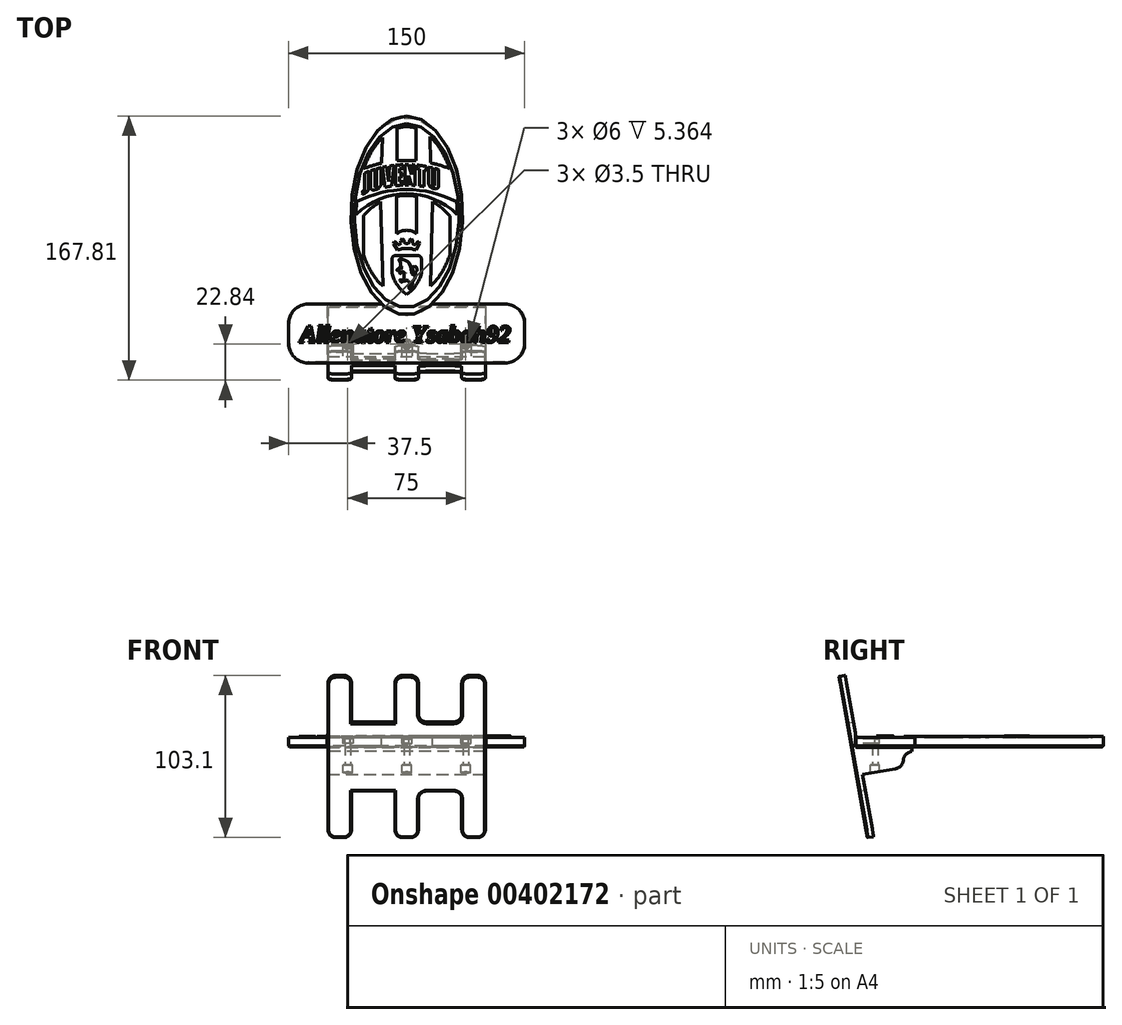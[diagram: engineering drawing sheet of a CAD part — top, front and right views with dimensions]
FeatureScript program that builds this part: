
annotation { "Feature Type Name" : "Feature", "Feature Type Description" : "" }
export const myFeature = defineFeature(function(context is Context, id is Id, definition is map)
    precondition{}
    {
        {
            var Q0;
            Q0=qCreatedBy(makeId("Top.planeOp"),FACE);
            var sketch = newSketch(context, id + "F0", { "sketchPlane" : qUnion([Q0])});
            skLineSegment(sketch, "E0", {"start": v(-0.23, 25.5) * mm, "end": v(16, 25.5) * mm, "construction": true});
            skLineSegment(sketch, "E1", {"start": v(0, -25.5) * mm, "end": v(11.3, -25.5) * mm, "construction": true});
            skLineSegment(sketch, "E2", {"start": v(14.52, 0) * mm, "end": v(14.52, -36.9) * mm, "construction": true});
            skLineSegment(sketch, "E3", {"start": v(-14.52, 0) * mm, "end": v(-14.52, -36.9) * mm, "construction": true});
            skEllipse(sketch, "E4", {"center": v(0, 0) * mm, "majorRadius": 14.2 * mm, "minorRadius": 25.29 * mm, "majorAxis": v(1, 0)});
            skEllipse(sketch, "E5", {"center": v(0, 0) * mm, "majorRadius": 13.32 * mm, "minorRadius": 23.36 * mm, "majorAxis": v(1, 0)});
            skEllipticalArc(sketch, "E6", {});
            skArc(sketch, "E7", {"start": v(-6.37, 13.3) * mm, "mid": v(-8.68, 12.68) * mm, "end": v(-10.93, 11.88) * mm});
            skLineSegment(sketch, "E8", {"start": v(-2.53, 14) * mm, "end": v(2.36, 14) * mm, "construction": true});
            skLineSegment(sketch, "E9", {"start": v(2.42, 22.16) * mm, "end": v(2.42, 13.9) * mm});
            skLineSegment(sketch, "E10", {"start": v(-2.48, 13.89) * mm, "end": v(-2.48, 22.14) * mm});
            skLineSegment(sketch, "E11", {"start": v(-6.2, 19.77) * mm, "end": v(-6.37, 13.3) * mm});
            skLineSegment(sketch, "E12", {"start": v(5.9, 20.05) * mm, "end": v(6, 13.37) * mm});
            skArc(sketch, "E13.trimOffspring", {"start": v(2.42, 13.9) * mm, "mid": v(-0.03, 14) * mm, "end": v(-2.48, 13.89) * mm});
            skEllipticalArc(sketch, "E14.trimOffspring", {});
            skArc(sketch, "E15.trimOffspring", {"start": v(10.93, 11.88) * mm, "mid": v(8.5, 12.73) * mm, "end": v(6, 13.37) * mm});
            skLineSegment(sketch, "E16", {"start": v(0, 6.57) * mm, "end": v(2.24, 6.57) * mm, "construction": true});
            skArc(sketch, "E17", {"start": v(12.7, 3.48) * mm, "mid": v(0, 6.57) * mm, "end": v(-12.7, 3.48) * mm});
            skLineSegment(sketch, "E18", {"start": v(0, 5.53) * mm, "end": v(1.97, 5.53) * mm, "construction": true});
            skArc(sketch, "E19", {"start": v(12.85, 0.22) * mm, "mid": v(0, 5.53) * mm, "end": v(-12.85, 0.22) * mm});
            skEllipticalArc(sketch, "E20.trimOffspring", {});
            skEllipticalArc(sketch, "E21.trimOffspring", {});
            skEllipticalArc(sketch, "E22", {});
            skLineSegment(sketch, "E23", {"start": v(0, 5.1) * mm, "end": v(2.87, 5.1) * mm, "construction": true});
            skLineSegment(sketch, "E24", {"start": v(11, -0.2) * mm, "end": v(11, -9.97) * mm});
            skLineSegment(sketch, "E25", {"start": v(6.52, 3.5) * mm, "end": v(6.04, -17.97) * mm});
            skLineSegment(sketch, "E26", {"start": v(-6.58, 3.47) * mm, "end": v(-6.04, -17.97) * mm});
            skLineSegment(sketch, "E27.MirrorCS", {"start": v(-11, -0.2) * mm, "end": v(-11, -9.97) * mm});
            skEllipticalArc(sketch, "E28.trimOffspring", {});
            skArc(sketch, "E29", {"start": v(2.52, -4.66) * mm, "mid": v(0, -3.77) * mm, "end": v(-2.52, -4.66) * mm});
            skLineSegment(sketch, "E30", {"start": v(2.52, 4.87) * mm, "end": v(2.52, -4.66) * mm});
            skLineSegment(sketch, "E31.MirrorCS", {"start": v(-2.52, 4.87) * mm, "end": v(-2.52, -4.66) * mm});
            skArc(sketch, "E32.trimOffspring", {"start": v(2.52, 4.87) * mm, "mid": v(0, 5.1) * mm, "end": v(-2.52, 4.87) * mm});
            skArc(sketch, "E33.trimOffspring", {"start": v(-6.58, 3.47) * mm, "mid": v(-8.99, 1.86) * mm, "end": v(-11, -0.2) * mm});
            skArc(sketch, "E34.trimOffspring", {"start": v(11, -0.2) * mm, "mid": v(8.96, 1.89) * mm, "end": v(6.52, 3.5) * mm});
            skEllipticalArc(sketch, "E35.trimOffspring", {});
            skArc(sketch, "E36", {"start": v(2.34, -8.82) * mm, "mid": v(0, -8.36) * mm, "end": v(-2.34, -8.82) * mm});
            skLineSegment(sketch, "E37", {"start": v(2.34, -8.82) * mm, "end": v(3.28, -7.14) * mm});
            skLineSegment(sketch, "E38", {"start": v(3.28, -7.14) * mm, "end": v(3.2, -6.62) * mm});
            skLineSegment(sketch, "E39", {"start": v(3.2, -6.62) * mm, "end": v(2.76, -6.8) * mm});
            skLineSegment(sketch, "E40", {"start": v(2.76, -6.8) * mm, "end": v(2.23, -7.36) * mm});
            skLineSegment(sketch, "E41", {"start": v(2.23, -7.36) * mm, "end": v(1.8, -7.36) * mm});
            skLineSegment(sketch, "E42", {"start": v(1.8, -7.36) * mm, "end": v(1.44, -7.04) * mm});
            skLineSegment(sketch, "E43", {"start": v(1.44, -7.04) * mm, "end": v(1.54, -6.32) * mm});
            skLineSegment(sketch, "E44", {"start": v(1.54, -6.32) * mm, "end": v(1.2, -5.88) * mm});
            skLineSegment(sketch, "E45", {"start": v(1.2, -5.88) * mm, "end": v(0.72, -6.24) * mm});
            skLineSegment(sketch, "E46", {"start": v(0.72, -6.24) * mm, "end": v(0.67, -6.78) * mm});
            skLineSegment(sketch, "E47", {"start": v(0.67, -6.78) * mm, "end": v(0.31, -7.14) * mm});
            skLineSegment(sketch, "E48", {"start": v(0.31, -7.14) * mm, "end": v(0, -7.14) * mm});
            skLineSegment(sketch, "E49", {"start": v(0, -8.36) * mm, "end": v(0, -5.24) * mm, "construction": true});
            skLineSegment(sketch, "E50.MirrorCS", {"start": v(-0.31, -7.14) * mm, "end": v(0, -7.14) * mm});
            skLineSegment(sketch, "E51.MirrorCS", {"start": v(-0.67, -6.78) * mm, "end": v(-0.31, -7.14) * mm});
            skLineSegment(sketch, "E52.MirrorCS", {"start": v(-0.72, -6.24) * mm, "end": v(-0.67, -6.78) * mm});
            skLineSegment(sketch, "E53.MirrorCS", {"start": v(-1.2, -5.88) * mm, "end": v(-0.72, -6.24) * mm});
            skLineSegment(sketch, "E54.MirrorCS", {"start": v(-1.54, -6.32) * mm, "end": v(-1.2, -5.88) * mm});
            skLineSegment(sketch, "E55.MirrorCS", {"start": v(-1.44, -7.04) * mm, "end": v(-1.54, -6.32) * mm});
            skLineSegment(sketch, "E56.MirrorCS", {"start": v(-1.8, -7.36) * mm, "end": v(-1.44, -7.04) * mm});
            skLineSegment(sketch, "E57.MirrorCS", {"start": v(-2.23, -7.36) * mm, "end": v(-1.8, -7.36) * mm});
            skLineSegment(sketch, "E58.MirrorCS", {"start": v(-2.76, -6.8) * mm, "end": v(-2.23, -7.36) * mm});
            skLineSegment(sketch, "E59.MirrorCS", {"start": v(-3.2, -6.62) * mm, "end": v(-2.76, -6.8) * mm});
            skLineSegment(sketch, "E60.MirrorCS", {"start": v(-2.34, -8.82) * mm, "end": v(-3.28, -7.14) * mm});
            skLineSegment(sketch, "E61.MirrorCS", {"start": v(-3.28, -7.14) * mm, "end": v(-3.2, -6.62) * mm});
            skLineSegment(sketch, "E62", {"start": v(3.75, -14.7) * mm, "end": v(3.75, -11.16) * mm});
            skLineSegment(sketch, "E63", {"start": v(0, -10.2) * mm, "end": v(3.06, -10.2) * mm});
            skArc(sketch, "E64", {"start": v(3.75, -11.16) * mm, "mid": v(3.57, -10.57) * mm, "end": v(3.06, -10.2) * mm});
            skLineSegment(sketch, "E65", {"start": v(0, -10.2) * mm, "end": v(0, -20.13) * mm, "construction": true});
            skArc(sketch, "E66.trimOffspring", {"start": v(0, -20.13) * mm, "mid": v(2.34, -17.73) * mm, "end": v(3.75, -14.7) * mm});
            skLineSegment(sketch, "E67.MirrorCS", {"start": v(-3.75, -14.7) * mm, "end": v(-3.75, -11.16) * mm});
            skLineSegment(sketch, "E68.MirrorCS", {"start": v(0, -10.2) * mm, "end": v(-3.06, -10.2) * mm});
            skArc(sketch, "E69.MirrorCS", {"start": v(-3.75, -11.16) * mm, "mid": v(-3.57, -10.57) * mm, "end": v(-3.06, -10.2) * mm});
            skArc(sketch, "E70.MirrorCS", {"start": v(0, -20.13) * mm, "mid": v(-2.34, -17.73) * mm, "end": v(-3.75, -14.7) * mm});
            skFitSpline(sketch, "E71", {"points": [v(2.15, -12.9) * mm, v(2.4, -13.22) * mm, v(2.4, -13.93) * mm, v(2.07, -13.78) * mm, v(1.97, -13.57) * mm, v(1.94, -13.4) * mm, v(1.95, -13.25) * mm, v(1.84, -13.17) * mm, v(1.77, -13.25) * mm, v(1.75, -13.35) * mm, v(1.76, -13.5) * mm, v(1.8, -13.68) * mm, v(1.9, -13.87) * mm, v(1.98, -14.07) * mm, v(2.08, -14.32) * mm, v(2.16, -14.54) * mm, v(2.2, -14.84) * mm, v(2.21, -14.95) * mm, v(2.27, -15.3) * mm, v(2.23, -15.56) * mm, v(2.12, -15.75) * mm, v(2.03, -15.92) * mm, v(1.95, -16.14) * mm, v(1.78, -16.38) * mm, v(1.73, -16.45) * mm, v(1.58, -16.7) * mm, v(1.5, -16.8) * mm, v(1.48, -16.97) * mm, v(1.5, -17.1) * mm, v(1.52, -17.2) * mm, v(1.62, -17.35) * mm, v(1.52, -17.51) * mm, v(1.31, -17.74) * mm, v(1.17, -17.96) * mm, v(1.12, -18.14) * mm, v(1.13, -18.28) * mm, v(1.24, -18.4) * mm, v(1.14, -18.66) * mm, v(1.03, -18.71) * mm, v(0.87, -18.73) * mm, v(0.69, -18.7) * mm, v(0.65, -18.63) * mm, v(0.63, -18.58) * mm, v(0.6, -18.5) * mm, v(0.57, -18.32) * mm, v(0.59, -18.14) * mm, v(0.61, -18.04) * mm, v(0.61, -17.96) * mm, v(0.63, -17.87) * mm, v(0.69, -17.8) * mm, v(0.77, -17.8) * mm, v(0.83, -17.76) * mm, v(0.83, -17.55) * mm, v(0.82, -17.33) * mm, v(0.74, -17.15) * mm, v(0.69, -17.06) * mm, v(0.64, -16.97) * mm, v(0.52, -16.78) * mm, v(0.44, -16.7) * mm, v(0.34, -16.53) * mm, v(0.26, -16.45) * mm, v(0.11, -16.36) * mm, v(0, -16.38) * mm, v(-0.12, -16.45) * mm, v(-0.27, -16.62) * mm, v(-0.38, -16.63) * mm, v(-0.61, -16.63) * mm, v(-0.63, -16.63) * mm], "startDerivative": vector(12.1, -9.46) * mm, "endDerivative": vector(-1.76, 0.05) * mm});
            skFitSpline(sketch, "E72", {"points": [v(-0.62, -16.63) * mm, v(-0.84, -16.63) * mm, v(-0.96, -16.63) * mm, v(-1.14, -16.63) * mm, v(-1.24, -16.65) * mm, v(-1.3, -16.74) * mm, v(-1.33, -16.89) * mm, v(-1.36, -16.97) * mm, v(-1.48, -17.04) * mm, v(-1.64, -17.01) * mm, v(-1.8, -16.91) * mm, v(-1.83, -16.76) * mm, v(-1.78, -16.57) * mm, v(-1.73, -16.45) * mm, v(-1.61, -16.36) * mm, v(-1.52, -16.3) * mm, v(-1.47, -16.28) * mm, v(-1.36, -16.27) * mm, v(-1.22, -16.2) * mm, v(-1.1, -16.19) * mm, v(-0.93, -16.18) * mm, v(-0.74, -16.17) * mm, v(-0.7, -15.94) * mm, v(-0.7, -15.8) * mm, v(-0.7, -15.55) * mm, v(-0.62, -15.33) * mm, v(-0.61, -15.15) * mm, v(-0.48, -14.95) * mm, v(0, -14.77) * mm, v(-0.51, -14.6) * mm, v(-0.67, -14.45) * mm, v(-0.87, -14.28) * mm, v(-1.05, -14.12) * mm, v(-1.23, -14.03) * mm, v(-1.32, -14.02) * mm, v(-1.4, -14.08) * mm, v(-1.43, -14.21) * mm, v(-1.35, -14.34) * mm, v(-1.24, -14.4) * mm, v(-1.17, -14.55) * mm, v(-1.2, -14.68) * mm, v(-1.24, -14.77) * mm, v(-1.35, -14.87) * mm, v(-1.48, -14.88) * mm, v(-1.6, -14.82) * mm, v(-1.75, -14.66) * mm, v(-1.8, -14.4) * mm, v(-1.78, -14.2) * mm, v(-1.74, -13.94) * mm, v(-1.8, -13.8) * mm, v(-1.85, -13.77) * mm, v(-1.97, -13.78) * mm, v(-2.07, -13.88) * mm, v(-2.11, -13.98) * mm, v(-2.15, -14.07) * mm, v(-2.2, -14.13) * mm, v(-2.35, -14.13) * mm, v(-2.4, -14.11) * mm, v(-2.48, -14.07) * mm, v(-2.52, -14) * mm, v(-2.53, -13.9) * mm, v(-2.48, -13.73) * mm, v(-2.42, -13.6) * mm, v(-2.38, -13.54) * mm, v(-2.28, -13.4) * mm, v(-2.15, -13.34) * mm, v(-2, -13.32) * mm, v(-1.93, -13.31) * mm, v(-1.86, -13.28) * mm, v(-1.83, -13.23) * mm, v(-1.78, -13.17) * mm, v(-1.68, -13.14) * mm, v(-1.56, -13.22) * mm, v(-1.44, -13.31) * mm, v(-1.29, -13.37) * mm, v(-1.24, -13.37) * mm, v(-1.14, -13.37) * mm, v(-1.05, -13.27) * mm, v(-1, -13.08) * mm, v(-1.08, -12.97) * mm, v(-1.3, -12.95) * mm, v(-1.42, -12.97) * mm, v(-1.52, -12.91) * mm, v(-1.54, -12.86) * mm, v(-1.58, -12.67) * mm, v(-1.56, -12.46) * mm, v(-1.53, -12.33) * mm, v(-1.5, -12.09) * mm, v(-1.49, -12.04) * mm, v(-1.53, -11.89) * mm, v(-1.64, -11.78) * mm, v(-1.66, -11.74) * mm, v(-1.73, -11.65) * mm, v(-1.75, -11.6) * mm, v(-1.77, -11.55) * mm, v(-1.8, -11.5) * mm, v(-1.84, -11.47) * mm, v(-1.94, -11.3) * mm, v(-1.94, -11.19) * mm, v(-1.81, -11.25) * mm, v(-1.76, -11.3) * mm, v(-1.66, -11.33) * mm, v(-1.62, -11.3) * mm, v(-1.68, -11.17) * mm, v(-1.73, -11.06) * mm, v(-1.73, -11) * mm, v(-1.64, -10.95) * mm, v(-1.6, -10.96) * mm, v(-1.47, -11.08) * mm, v(-1.33, -11.15) * mm, v(-1.1, -11.24) * mm, v(-0.94, -11.26) * mm, v(-0.71, -11.32) * mm, v(-0.58, -11.35) * mm, v(-0.41, -11.4) * mm, v(-0.25, -11.44) * mm, v(-0.2, -11.45) * mm, v(-0.12, -11.47) * mm, v(0.22, -11.64) * mm, v(0.43, -11.77) * mm, v(0.48, -11.8) * mm, v(0.54, -11.89) * mm, v(0.58, -11.93) * mm, v(0.63, -12.01) * mm, v(0.69, -12.14) * mm, v(0.72, -12.18) * mm, v(0.77, -12.32) * mm, v(0.96, -12.83) * mm, v(1.03, -13.13) * mm, v(1.15, -13.66) * mm, v(1.2, -13.92) * mm, v(1.22, -14.1) * mm, v(1.23, -14.25) * mm, v(1.32, -14.64) * mm, v(1.4, -14.83) * mm, v(1.47, -14.98) * mm, v(1.53, -15.05) * mm, v(1.64, -15.08) * mm, v(1.68, -15.08) * mm, v(1.74, -15.08) * mm, v(1.86, -15) * mm, v(1.87, -14.95) * mm, v(1.85, -14.8) * mm, v(1.8, -14.69) * mm, v(1.78, -14.65) * mm, v(1.75, -14.57) * mm, v(1.7, -14.39) * mm, v(1.67, -14.33) * mm, v(1.63, -14.25) * mm, v(1.61, -14.2) * mm, v(1.5, -13.89) * mm, v(1.5, -13.78) * mm, v(1.45, -13.6) * mm, v(1.44, -13.49) * mm, v(1.41, -13.3) * mm, v(1.42, -13.23) * mm, v(1.42, -13.15) * mm, v(1.44, -13.08) * mm, v(1.45, -13.04) * mm, v(1.55, -12.84) * mm, v(1.65, -12.79) * mm, v(1.72, -12.76) * mm, v(1.87, -12.77) * mm, v(1.97, -12.8) * mm, v(2.06, -12.84) * mm, v(2.15, -12.9) * mm, v(2.42, -12.97) * mm, v(2.42, -12.97) * mm], "startDerivative": vector(-31.58, 0.07) * mm, "endDerivative": vector(-2, 3.85) * mm});
            skLineSegment(sketch, "E73", {"start": v(0, 12.9) * mm, "end": v(-3.21, 12.9) * mm, "construction": true});
            skArc(sketch, "E74", {"start": v(8.14, 11.68) * mm, "mid": v(7.62, 11.83) * mm, "end": v(7.1, 11.98) * mm});
            skLineSegment(sketch, "E75", {"start": v(0, 7.7) * mm, "end": v(-5.8, 7.7) * mm, "construction": true});
            skArc(sketch, "E76", {"start": v(9.94, 5.87) * mm, "mid": v(9.85, 5.9) * mm, "end": v(9.77, 5.94) * mm});
            skLineSegment(sketch, "E77", {"start": v(2.17, 12.82) * mm, "end": v(2.17, 7.62) * mm});
            skLineSegment(sketch, "E78", {"start": v(-0.35, 12.9) * mm, "end": v(-0.35, 7.7) * mm});
            skLineSegment(sketch, "E79", {"start": v(0.45, 7.7) * mm, "end": v(0.45, 10.18) * mm});
            skLineSegment(sketch, "E80", {"start": v(0.45, 10.18) * mm, "end": v(1.28, 7.68) * mm});
            skLineSegment(sketch, "E81", {"start": v(0.45, 12.9) * mm, "end": v(1.28, 10.38) * mm});
            skLineSegment(sketch, "E82", {"start": v(1.28, 10.38) * mm, "end": v(1.35, 12.87) * mm});
            skLineSegment(sketch, "E83", {"start": v(5.54, 12.34) * mm, "end": v(5.54, 8.18) * mm});
            skLineSegment(sketch, "E84", {"start": v(6.6, 12.1) * mm, "end": v(6.6, 8.03) * mm});
            skLineSegment(sketch, "E85", {"start": v(7.1, 11.98) * mm, "end": v(7.1, 7.96) * mm});
            skLineSegment(sketch, "E86", {"start": v(8.14, 11.68) * mm, "end": v(8.14, 7.6) * mm});
            skLineSegment(sketch, "E87", {"start": v(2.62, 12.78) * mm, "end": v(2.62, 11.93) * mm});
            skLineSegment(sketch, "E88", {"start": v(2.62, 11.93) * mm, "end": v(3.33, 11.8) * mm});
            skLineSegment(sketch, "E89", {"start": v(3.33, 11.8) * mm, "end": v(3.33, 7.5) * mm});
            skLineSegment(sketch, "E90", {"start": v(5.1, 12.43) * mm, "end": v(5.1, 11.4) * mm});
            skLineSegment(sketch, "E91", {"start": v(5.1, 11.4) * mm, "end": v(4.43, 11.57) * mm});
            skLineSegment(sketch, "E92", {"start": v(4.43, 11.57) * mm, "end": v(4.43, 7.35) * mm});
            skLineSegment(sketch, "E93", {"start": v(-0.97, 12.89) * mm, "end": v(-0.97, 11.95) * mm});
            skLineSegment(sketch, "E94", {"start": v(-0.97, 11.95) * mm, "end": v(-1.77, 11.95) * mm});
            skLineSegment(sketch, "E95", {"start": v(-1.77, 11.95) * mm, "end": v(-1.77, 10.76) * mm});
            skLineSegment(sketch, "E96", {"start": v(-1.77, 10.76) * mm, "end": v(-1.02, 10.76) * mm});
            skLineSegment(sketch, "E97", {"start": v(-1.02, 10.76) * mm, "end": v(-1.02, 9.87) * mm});
            skLineSegment(sketch, "E98", {"start": v(-1.02, 9.87) * mm, "end": v(-1.77, 9.87) * mm});
            skLineSegment(sketch, "E99", {"start": v(-1.77, 9.87) * mm, "end": v(-1.77, 8.6) * mm});
            skLineSegment(sketch, "E100", {"start": v(-1.77, 8.6) * mm, "end": v(-0.86, 8.6) * mm});
            skLineSegment(sketch, "E101", {"start": v(-0.86, 8.6) * mm, "end": v(-0.86, 7.7) * mm});
            skLineSegment(sketch, "E102", {"start": v(-2.85, 12.76) * mm, "end": v(-2.85, 7.56) * mm});
            skLineSegment(sketch, "E103", {"start": v(-10.74, 10.74) * mm, "end": v(-10.74, 6.6) * mm});
            skLineSegment(sketch, "E104", {"start": v(-9.68, 11.16) * mm, "end": v(-9.68, 6.66) * mm});
            skLineSegment(sketch, "E105", {"start": v(-9.17, 11.34) * mm, "end": v(-9.17, 7.24) * mm});
            skLineSegment(sketch, "E106", {"start": v(-8.07, 11.7) * mm, "end": v(-8.07, 7.5) * mm});
            skLineSegment(sketch, "E107", {"start": v(-7.6, 11.84) * mm, "end": v(-7.6, 7.62) * mm});
            skLineSegment(sketch, "E108", {"start": v(-6.52, 12.12) * mm, "end": v(-6.52, 7.7) * mm});
            skLineSegment(sketch, "E109", {"start": v(-6.17, 12.2) * mm, "end": v(-5.5, 7.16) * mm});
            skLineSegment(sketch, "E110", {"start": v(-3.2, 12.72) * mm, "end": v(-3.8, 7.45) * mm});
            skLineSegment(sketch, "E111", {"start": v(-4.3, 12.57) * mm, "end": v(-4.67, 8.56) * mm});
            skLineSegment(sketch, "E112", {"start": v(-4.67, 8.56) * mm, "end": v(-5.13, 12.43) * mm});
            skFitSpline(sketch, "E113", {"points": [v(11, 9.2) * mm, v(10.12, 9.56) * mm, v(10.11, 9.69) * mm, v(10.1, 9.76) * mm, v(10.12, 9.93) * mm, v(10.12, 10.05) * mm, v(10.09, 10.2) * mm, v(10.06, 10.32) * mm, v(10, 10.4) * mm, v(9.94, 10.45) * mm, v(9.83, 10.5) * mm, v(9.68, 10.48) * mm, v(9.6, 10.38) * mm, v(9.57, 10.23) * mm, v(9.56, 10.1) * mm, v(9.54, 9.85) * mm, v(9.54, 9.78) * mm, v(9.54, 9.67) * mm, v(9.56, 9.62) * mm, v(9.6, 9.5) * mm, v(9.63, 9.46) * mm, v(9.7, 9.36) * mm, v(9.72, 9.3) * mm, v(9.78, 9.22) * mm, v(9.82, 9.17) * mm, v(9.91, 9.08) * mm, v(10.02, 8.98) * mm, v(10.06, 8.93) * mm, v(10.1, 8.87) * mm, v(10.15, 8.81) * mm, v(10.24, 8.73) * mm, v(10.4, 8.6) * mm, v(10.57, 8.4) * mm, v(10.68, 8.25) * mm, v(10.72, 8.19) * mm, v(10.8, 8.08) * mm, v(10.86, 7.98) * mm, v(10.94, 7.84) * mm, v(10.98, 7.76) * mm, v(11.04, 7.62) * mm, v(11.09, 7.5) * mm, v(11.1, 7.43) * mm, v(11.11, 7.07) * mm, v(11.11, 6.9) * mm, v(11.1, 6.8) * mm, v(11.09, 6.66) * mm, v(11.08, 6.58) * mm, v(11.07, 6.43) * mm, v(11.05, 6.37) * mm, v(11.04, 6.24) * mm, v(11.02, 6.16) * mm, v(11, 6.07) * mm, v(10.93, 5.92) * mm, v(10.85, 5.86) * mm, v(10.72, 5.82) * mm, v(10.55, 5.8) * mm, v(10.41, 5.8) * mm, v(10.24, 5.8) * mm, v(10.15, 5.82) * mm, v(9.94, 5.87) * mm, v(9.77, 5.94) * mm, v(9.49, 6.05) * mm, v(9.4, 6.13) * mm, v(9.32, 6.2) * mm, v(9.22, 6.3) * mm, v(9.15, 6.34) * mm, v(9.1, 6.39) * mm, v(9.04, 6.47) * mm, v(9, 6.53) * mm, v(8.9, 6.66) * mm, v(8.87, 6.72) * mm, v(8.82, 6.78) * mm, v(8.8, 6.83) * mm, v(8.75, 6.93) * mm, v(8.73, 7) * mm, v(8.7, 7.07) * mm, v(8.67, 7.19) * mm, v(8.67, 7.25) * mm, v(8.67, 7.52) * mm, v(8.71, 7.83) * mm, v(8.72, 7.91) * mm, v(8.77, 8) * mm, v(8.9, 7.99) * mm, v(9.03, 7.95) * mm, v(9.19, 7.89) * mm, v(9.25, 7.85) * mm, v(9.35, 7.81) * mm, v(9.48, 7.77) * mm, v(9.56, 7.71) * mm, v(9.6, 7.64) * mm, v(9.63, 7.58) * mm, v(9.64, 7.48) * mm, v(9.64, 7.4) * mm, v(9.64, 7.29) * mm, v(9.63, 7.2) * mm, v(9.63, 7.11) * mm, v(9.63, 7.04) * mm, v(9.63, 6.96) * mm, v(9.63, 6.9) * mm, v(9.65, 6.83) * mm, v(9.69, 6.74) * mm, v(9.75, 6.63) * mm, v(9.8, 6.57) * mm, v(9.88, 6.55) * mm, v(10, 6.58) * mm, v(10.11, 6.69) * mm, v(10.15, 6.78) * mm, v(10.17, 6.83) * mm, v(10.19, 6.94) * mm, v(10.19, 7.01) * mm, v(10.17, 7.13) * mm, v(10.17, 7.21) * mm, v(10.15, 7.33) * mm, v(10.14, 7.42) * mm, v(10.11, 7.54) * mm, v(10.08, 7.6) * mm, v(10.05, 7.7) * mm, v(10.01, 7.74) * mm, v(9.98, 7.8) * mm, v(9.94, 7.85) * mm, v(9.87, 7.94) * mm, v(9.82, 8) * mm, v(9.74, 8.1) * mm, v(9.7, 8.15) * mm, v(9.65, 8.21) * mm, v(9.6, 8.26) * mm, v(9.51, 8.3) * mm, v(9.29, 8.59) * mm, v(9.18, 8.73) * mm, v(9.15, 8.8) * mm, v(9.07, 8.91) * mm, v(8.99, 9.01) * mm, v(8.96, 9.07) * mm, v(8.92, 9.14) * mm, v(8.77, 9.46) * mm, v(8.71, 9.62) * mm, v(8.7, 9.68) * mm, v(8.68, 9.78) * mm, v(8.68, 9.9) * mm, v(8.68, 9.97) * mm, v(8.68, 10.04) * mm, v(8.69, 10.1) * mm, v(8.69, 10.17) * mm, v(8.68, 10.35) * mm, v(8.68, 10.46) * mm, v(8.68, 10.6) * mm, v(8.67, 10.7) * mm, v(8.72, 10.84) * mm, v(8.77, 10.98) * mm, v(8.79, 11.04) * mm, v(8.84, 11.12) * mm, v(8.93, 11.16) * mm, v(9.1, 11.24) * mm, v(9.32, 11.3) * mm, v(9.53, 11.3) * mm, v(9.79, 11.28) * mm, v(9.85, 11.26) * mm, v(10.01, 11.2) * mm, v(10.08, 11.17) * mm, v(10.2, 11.11) * mm, v(10.24, 11.07) * mm, v(10.3, 11.02) * mm, v(10.61, 10.69) * mm, v(10.74, 10.57) * mm, v(10.85, 10.42) * mm, v(10.97, 10.18) * mm, v(11, 10.12) * mm, v(11.02, 10.06) * mm, v(11.06, 9.84) * mm, v(11.06, 9.74) * mm, v(11.06, 9.64) * mm, v(11.06, 9.57) * mm, v(11.05, 9.48) * mm, v(11.04, 9.41) * mm, v(11.02, 9.31) * mm, v(11, 9.2) * mm]});
            skFitSpline(sketch, "E114", {"points": [v(7.1, 7.96) * mm, v(7.1, 7.75) * mm, v(7.03, 7.6) * mm, v(6.84, 7.55) * mm, v(6.8, 7.55) * mm, v(6.67, 7.6) * mm, v(6.57, 7.74) * mm, v(6.57, 7.96) * mm, v(6.6, 8.03) * mm], "startDerivative": vector(0.07, -1.41) * mm, "endDerivative": vector(0.28, 0.67) * mm});
            skFitSpline(sketch, "E115", {"points": [v(8.14, 7.6) * mm, v(8.08, 7.24) * mm, v(7.82, 6.95) * mm, v(7.53, 6.8) * mm, v(7.14, 6.8) * mm, v(6.6, 6.91) * mm, v(6.23, 7.1) * mm, v(6.01, 7.29) * mm, v(5.77, 7.6) * mm, v(5.63, 7.92) * mm, v(5.54, 8.18) * mm], "startDerivative": vector(-0.1, -3.84) * mm, "endDerivative": vector(-1, 2.94) * mm});
            skFitSpline(sketch, "E116", {"points": [v(-9.68, 6.66) * mm, v(-9.75, 6.48) * mm, v(-9.9, 6.22) * mm, v(-10, 6.08) * mm, v(-10.25, 5.87) * mm, v(-10.4, 5.73) * mm, v(-10.51, 5.64) * mm, v(-10.73, 5.55) * mm], "startDerivative": vector(-0.45, -1.23) * mm, "endDerivative": vector(-1.6, -0.63) * mm});
            skFitSpline(sketch, "E117", {"points": [v(-11.2, 5.36) * mm, v(-11.16, 5.62) * mm, v(-11.16, 6.14) * mm, v(-10.97, 6.26) * mm, v(-10.88, 6.31) * mm, v(-10.79, 6.42) * mm, v(-10.75, 6.5) * mm, v(-10.74, 6.6) * mm, v(-10.74, 6.99) * mm], "startDerivative": vector(0.34, 1.65) * mm, "endDerivative": vector(-0.03, 2.69) * mm});
            skFitSpline(sketch, "E118", {"points": [v(-9.17, 7.24) * mm, v(-9.1, 6.91) * mm, v(-9.03, 6.76) * mm, v(-8.83, 6.6) * mm, v(-8.4, 6.45) * mm, v(-7.88, 6.57) * mm, v(-7.27, 6.77) * mm, v(-7.03, 6.99) * mm, v(-6.8, 7.3) * mm, v(-6.6, 7.6) * mm, v(-6.52, 7.7) * mm], "startDerivative": vector(0.5, -3.69) * mm, "endDerivative": vector(1.09, 1.44) * mm});
            skFitSpline(sketch, "E119", {"points": [v(-7.6, 7.62) * mm, v(-7.6, 7.47) * mm, v(-7.67, 7.35) * mm, v(-7.86, 7.24) * mm, v(-8.04, 7.32) * mm, v(-8.07, 7.5) * mm], "startDerivative": vector(0.09, -0.84) * mm, "endDerivative": vector(0.02, 0.91) * mm});
            skArc(sketch, "E120.trimOffspring", {"start": v(-10.51, 5.64) * mm, "mid": v(-10.86, 5.5) * mm, "end": v(-11.2, 5.36) * mm});
            skArc(sketch, "E121.trimOffspring", {"start": v(-9.68, 11.16) * mm, "mid": v(-10.2, 10.95) * mm, "end": v(-10.74, 10.74) * mm});
            skArc(sketch, "E122.trimOffspring", {"start": v(-7.88, 6.57) * mm, "mid": v(-8.05, 6.52) * mm, "end": v(-8.2, 6.47) * mm});
            skArc(sketch, "E123.trimOffspring", {"start": v(-3.8, 7.45) * mm, "mid": v(-4.65, 7.31) * mm, "end": v(-5.5, 7.16) * mm});
            skArc(sketch, "E124.trimOffspring", {"start": v(-0.86, 7.7) * mm, "mid": v(-1.85, 7.64) * mm, "end": v(-2.85, 7.56) * mm});
            skArc(sketch, "E125.trimOffspring", {"start": v(0.45, 7.7) * mm, "mid": v(0.05, 7.7) * mm, "end": v(-0.35, 7.7) * mm});
            skArc(sketch, "E126.trimOffspring", {"start": v(2.17, 7.62) * mm, "mid": v(1.73, 7.65) * mm, "end": v(1.28, 7.68) * mm});
            skArc(sketch, "E127.trimOffspring", {"start": v(4.43, 7.35) * mm, "mid": v(3.88, 7.43) * mm, "end": v(3.33, 7.5) * mm});
            skArc(sketch, "E128.trimOffspring", {"start": v(6.84, 6.85) * mm, "mid": v(6.72, 6.88) * mm, "end": v(6.6, 6.91) * mm});
            skArc(sketch, "E129.trimOffspring", {"start": v(5.1, 12.43) * mm, "mid": v(3.87, 12.63) * mm, "end": v(2.62, 12.78) * mm});
            skArc(sketch, "E130.trimOffspring", {"start": v(0.45, 12.9) * mm, "mid": v(0.05, 12.9) * mm, "end": v(-0.35, 12.9) * mm});
            skArc(sketch, "E131.trimOffspring", {"start": v(-0.97, 12.89) * mm, "mid": v(-1.9, 12.84) * mm, "end": v(-2.85, 12.76) * mm});
            skArc(sketch, "E132.trimOffspring", {"start": v(-3.2, 12.72) * mm, "mid": v(-3.75, 12.65) * mm, "end": v(-4.3, 12.57) * mm});
            skArc(sketch, "E133.trimOffspring", {"start": v(-5.13, 12.43) * mm, "mid": v(-5.65, 12.32) * mm, "end": v(-6.17, 12.2) * mm});
            skArc(sketch, "E134.trimOffspring", {"start": v(-6.52, 12.12) * mm, "mid": v(-7.06, 11.99) * mm, "end": v(-7.6, 11.84) * mm});
            skArc(sketch, "E135.trimOffspring", {"start": v(-8.07, 11.7) * mm, "mid": v(-8.62, 11.53) * mm, "end": v(-9.17, 11.34) * mm});
            skArc(sketch, "E136.trimOffspring", {"start": v(2.17, 12.82) * mm, "mid": v(1.76, 12.85) * mm, "end": v(1.35, 12.87) * mm});
            skLineSegment(sketch, "E137", {"start": v(5.54, 12.34) * mm, "end": v(6.6, 12.1) * mm});
            const initialGuessF0  = {"E6": [0, 0, 0, 1, 0.022562885147601155, 0.012851271823588573, 0.502769524575932, 1.0162238153190999], "E14.trimOffspring": [0, 0, 0, 1, 0.022562885147601155, 0.012851271823588573, 6.094011800529932, 0.19398440980100293], "E20.trimOffspring": [0, 0, 0, 1, 0.022562885147601155, 0.012851271823588573, 5.266961491860487, 5.806421527511528], "E21.trimOffspring": [0, 0, 0, 1, 0.022562885147601155, 0.012851271823588573, 1.4158842663045312, 1.5611346644012138], "E22": [0, 0, 0, -1, 0.020476011405082317, 0.01260289410030643, 0.49992463143607707, 1.0622472341800782], "E28.trimOffspring": [0, 0, 0, -1, 0.020476011405082317, 0.01260289410030643, 5.220938072999507, 5.783566470268216], "E35.trimOffspring": [0, 0, 0, 1, 0.022562885147601155, 0.012851271823588573, 4.722050642778372, 4.867301040875056]};
            skSetInitialGuess(sketch, initialGuessF0);
            skSolve(sketch);
        }
        {
            var Q0;
            Q0=qCreatedBy(makeId("Top.planeOp"),FACE);
            var sketch = newSketch(context, id + "F1", { "sketchPlane" : qUnion([Q0])});
            skEllipse(sketch, "E138.0", {"center": v(0, 0) * mm, "majorRadius": 25.29 * mm, "minorRadius": 14.2 * mm, "majorAxis": v(0, 1)});
            skSolve(sketch);
        }
        {
            var Q0;
            Q0 = qSketchRegion(id + "F1", true);
            extrude(context, id + "F2", {"entities" : qUnion([Q0]), "depth" : 2 * mm});
        }
        {
            var Q0;
            Q0=makeQuery(id+"F2.opExtrude","CAP_FACE",FACE,{"disambiguationData":[OSD([sQuery(id+"F1.wireOp",EDGE,"E138.0")])],"isStart":false});
            var sketch = newSketch(context, id + "F3", { "sketchPlane" : qUnion([Q0])});
            skLineSegment(sketch, "E139.0", {"start": v(-2.52, 4.87) * mm, "end": v(-2.52, -4.66) * mm});
            skLineSegment(sketch, "E139.1", {"start": v(3.33, 11.8) * mm, "end": v(3.33, 7.5) * mm});
            skLineSegment(sketch, "E139.2", {"start": v(0.45, 10.18) * mm, "end": v(1.28, 7.68) * mm});
            skLineSegment(sketch, "E139.3", {"start": v(-9.17, 11.34) * mm, "end": v(-9.17, 7.24) * mm});
            skArc(sketch, "E139.4", {"start": v(2.34, -8.82) * mm, "mid": v(0, -8.36) * mm, "end": v(-2.34, -8.82) * mm});
            skArc(sketch, "E139.5", {"start": v(10.93, 11.88) * mm, "mid": v(8.5, 12.73) * mm, "end": v(6, 13.37) * mm});
            skArc(sketch, "E139.6", {"start": v(2.52, 4.87) * mm, "mid": v(0, 5.1) * mm, "end": v(-2.52, 4.87) * mm});
            skLineSegment(sketch, "E139.7", {"start": v(0.45, 7.7) * mm, "end": v(0.45, 10.18) * mm});
            skLineSegment(sketch, "E139.8", {"start": v(-4.67, 8.56) * mm, "end": v(-5.13, 12.43) * mm});
            skLineSegment(sketch, "E139.9", {"start": v(0, -10.2) * mm, "end": v(3.06, -10.2) * mm});
            skLineSegment(sketch, "E139.10", {"start": v(-4.3, 12.57) * mm, "end": v(-4.67, 8.56) * mm});
            skLineSegment(sketch, "E139.12", {"start": v(6.52, 3.5) * mm, "end": v(6.04, -17.97) * mm});
            skLineSegment(sketch, "E139.13", {"start": v(11, -0.2) * mm, "end": v(11, -9.97) * mm});
            skLineSegment(sketch, "E139.14", {"start": v(-6.58, 3.47) * mm, "end": v(-6.04, -17.97) * mm});
            skLineSegment(sketch, "E139.15", {"start": v(-9.68, 11.16) * mm, "end": v(-9.68, 6.66) * mm});
            skLineSegment(sketch, "E139.16", {"start": v(-2.85, 12.76) * mm, "end": v(-2.85, 7.56) * mm});
            skLineSegment(sketch, "E139.17", {"start": v(-3.2, 12.72) * mm, "end": v(-3.8, 7.45) * mm});
            skLineSegment(sketch, "E139.18", {"start": v(2.52, 4.87) * mm, "end": v(2.52, -4.66) * mm});
            skLineSegment(sketch, "E139.19", {"start": v(3.75, -14.7) * mm, "end": v(3.75, -11.16) * mm});
            skLineSegment(sketch, "E139.20", {"start": v(-8.07, 11.7) * mm, "end": v(-8.07, 7.5) * mm});
            skLineSegment(sketch, "E139.21", {"start": v(-11, -0.2) * mm, "end": v(-11, -9.97) * mm});
            skLineSegment(sketch, "E139.22", {"start": v(-7.6, 11.84) * mm, "end": v(-7.6, 7.62) * mm});
            skLineSegment(sketch, "E139.23", {"start": v(2.42, 22.16) * mm, "end": v(2.42, 13.9) * mm});
            skLineSegment(sketch, "E139.24", {"start": v(-2.48, 13.89) * mm, "end": v(-2.48, 22.14) * mm});
            skLineSegment(sketch, "E139.25", {"start": v(-6.2, 19.77) * mm, "end": v(-6.37, 13.3) * mm});
            skEllipse(sketch, "E139.28", {"center": v(0, 0) * mm, "majorRadius": 25.29 * mm, "minorRadius": 14.2 * mm, "majorAxis": v(0, 1)});
            skEllipse(sketch, "E139.29", {"center": v(0, 0) * mm, "majorRadius": 23.36 * mm, "minorRadius": 13.32 * mm, "majorAxis": v(0, 1)});
            skEllipticalArc(sketch, "E139.30", {});
            skArc(sketch, "E139.31", {"start": v(-6.37, 13.3) * mm, "mid": v(-8.68, 12.68) * mm, "end": v(-10.93, 11.88) * mm});
            skArc(sketch, "E139.32", {"start": v(-0.86, 7.7) * mm, "mid": v(-1.85, 7.64) * mm, "end": v(-2.85, 7.56) * mm});
            skLineSegment(sketch, "E139.33", {"start": v(-6.52, 12.12) * mm, "end": v(-6.52, 7.7) * mm});
            skLineSegment(sketch, "E139.34", {"start": v(4.43, 11.57) * mm, "end": v(4.43, 7.35) * mm});
            skEllipticalArc(sketch, "E139.35", {});
            skArc(sketch, "E139.36", {"start": v(0, -20.13) * mm, "mid": v(2.34, -17.73) * mm, "end": v(3.75, -14.7) * mm});
            skLineSegment(sketch, "E139.37", {"start": v(5.9, 20.05) * mm, "end": v(6, 13.37) * mm});
            skEllipticalArc(sketch, "E139.38", {});
            skLineSegment(sketch, "E139.39", {"start": v(0.45, 12.9) * mm, "end": v(1.28, 10.38) * mm});
            skLineSegment(sketch, "E139.40", {"start": v(-6.17, 12.2) * mm, "end": v(-5.5, 7.16) * mm});
            skLineSegment(sketch, "E139.41", {"start": v(-10.74, 10.74) * mm, "end": v(-10.74, 6.6) * mm});
            skArc(sketch, "E139.42", {"start": v(2.52, -4.66) * mm, "mid": v(0, -3.77) * mm, "end": v(-2.52, -4.66) * mm});
            skLineSegment(sketch, "E139.43", {"start": v(2.17, 12.82) * mm, "end": v(2.17, 7.62) * mm});
            skArc(sketch, "E139.44", {"start": v(2.42, 13.9) * mm, "mid": v(-0.03, 14) * mm, "end": v(-2.48, 13.89) * mm});
            skArc(sketch, "E139.45", {"start": v(12.7, 3.48) * mm, "mid": v(0, 6.57) * mm, "end": v(-12.7, 3.48) * mm});
            skArc(sketch, "E139.46", {"start": v(-6.58, 3.47) * mm, "mid": v(-8.99, 1.86) * mm, "end": v(-11, -0.2) * mm});
            skEllipticalArc(sketch, "E139.47", {});
            skArc(sketch, "E139.48", {"start": v(12.85, 0.22) * mm, "mid": v(0, 5.53) * mm, "end": v(-12.85, 0.22) * mm});
            skLineSegment(sketch, "E139.49", {"start": v(5.54, 12.34) * mm, "end": v(5.54, 8.18) * mm});
            skLineSegment(sketch, "E139.50", {"start": v(-3.75, -14.7) * mm, "end": v(-3.75, -11.16) * mm});
            skEllipticalArc(sketch, "E139.51", {});
            skLineSegment(sketch, "E139.52", {"start": v(6.6, 12.1) * mm, "end": v(6.6, 8.03) * mm});
            skLineSegment(sketch, "E139.53", {"start": v(0, -10.2) * mm, "end": v(-3.06, -10.2) * mm});
            skLineSegment(sketch, "E139.54", {"start": v(7.1, 11.98) * mm, "end": v(7.1, 7.96) * mm});
            skEllipticalArc(sketch, "E139.55", {});
            skEllipticalArc(sketch, "E139.56", {});
            skArc(sketch, "E139.57", {"start": v(0, -20.13) * mm, "mid": v(-2.34, -17.73) * mm, "end": v(-3.75, -14.7) * mm});
            skLineSegment(sketch, "E139.58", {"start": v(1.28, 10.38) * mm, "end": v(1.35, 12.87) * mm});
            skArc(sketch, "E139.60", {"start": v(-0.97, 12.89) * mm, "mid": v(-1.9, 12.84) * mm, "end": v(-2.85, 12.76) * mm});
            skArc(sketch, "E139.61", {"start": v(11, -0.2) * mm, "mid": v(8.96, 1.89) * mm, "end": v(6.52, 3.5) * mm});
            skArc(sketch, "E139.62", {"start": v(5.1, 12.43) * mm, "mid": v(3.87, 12.63) * mm, "end": v(2.62, 12.78) * mm});
            skFitSpline(sketch, "E139.63", {"points": [v(11, 9.2) * mm, v(10.87, 9.15) * mm, v(10, 9.5) * mm, v(10.13, 9.69) * mm, v(10.1, 9.76) * mm, v(10.13, 9.94) * mm, v(10.13, 10.05) * mm, v(10.08, 10.2) * mm, v(10.07, 10.32) * mm, v(9.99, 10.4) * mm, v(9.94, 10.46) * mm, v(9.83, 10.52) * mm, v(9.68, 10.5) * mm, v(9.57, 10.39) * mm, v(9.57, 10.22) * mm, v(9.55, 10.1) * mm, v(9.54, 9.85) * mm, v(9.53, 9.78) * mm, v(9.54, 9.67) * mm, v(9.56, 9.62) * mm, v(9.6, 9.5) * mm, v(9.63, 9.46) * mm, v(9.7, 9.35) * mm, v(9.72, 9.3) * mm, v(9.78, 9.22) * mm, v(9.81, 9.17) * mm, v(9.91, 9.08) * mm, v(10.02, 8.98) * mm, v(10.05, 8.93) * mm, v(10.1, 8.87) * mm, v(10.16, 8.8) * mm, v(10.24, 8.72) * mm, v(10.41, 8.6) * mm, v(10.56, 8.41) * mm, v(10.68, 8.26) * mm, v(10.71, 8.19) * mm, v(10.81, 8.08) * mm, v(10.85, 7.98) * mm, v(10.95, 7.84) * mm, v(10.97, 7.76) * mm, v(11.04, 7.63) * mm, v(11.09, 7.49) * mm, v(11.1, 7.44) * mm, v(11.11, 7.07) * mm, v(11.11, 6.9) * mm, v(11.1, 6.8) * mm, v(11.09, 6.66) * mm, v(11.08, 6.59) * mm, v(11.08, 6.43) * mm, v(11.05, 6.37) * mm, v(11.05, 6.24) * mm, v(11.01, 6.16) * mm, v(11.01, 6.07) * mm, v(10.94, 5.92) * mm, v(10.86, 5.85) * mm, v(10.72, 5.82) * mm, v(10.54, 5.79) * mm, v(10.42, 5.8) * mm, v(10.23, 5.8) * mm, v(10.15, 5.81) * mm, v(9.93, 5.87) * mm, v(9.78, 5.94) * mm, v(9.48, 6.04) * mm, v(9.4, 6.13) * mm, v(9.32, 6.2) * mm, v(9.23, 6.3) * mm, v(9.14, 6.34) * mm, v(9.1, 6.39) * mm, v(9.04, 6.47) * mm, v(9, 6.53) * mm, v(8.9, 6.66) * mm, v(8.87, 6.72) * mm, v(8.82, 6.79) * mm, v(8.8, 6.83) * mm, v(8.75, 6.94) * mm, v(8.74, 7) * mm, v(8.69, 7.07) * mm, v(8.66, 7.19) * mm, v(8.67, 7.26) * mm, v(8.66, 7.52) * mm, v(8.72, 7.83) * mm, v(8.71, 7.9) * mm, v(8.76, 8.04) * mm, v(8.9, 7.98) * mm, v(9.02, 7.95) * mm, v(9.19, 7.9) * mm, v(9.25, 7.86) * mm, v(9.35, 7.8) * mm, v(9.48, 7.78) * mm, v(9.56, 7.72) * mm, v(9.6, 7.64) * mm, v(9.63, 7.59) * mm, v(9.65, 7.48) * mm, v(9.64, 7.4) * mm, v(9.65, 7.28) * mm, v(9.62, 7.2) * mm, v(9.63, 7.11) * mm, v(9.62, 7.05) * mm, v(9.63, 6.96) * mm, v(9.62, 6.9) * mm, v(9.66, 6.83) * mm, v(9.68, 6.73) * mm, v(9.75, 6.64) * mm, v(9.8, 6.56) * mm, v(9.88, 6.55) * mm, v(10, 6.56) * mm, v(10.12, 6.68) * mm, v(10.15, 6.78) * mm, v(10.18, 6.83) * mm, v(10.19, 6.94) * mm, v(10.2, 7.01) * mm, v(10.16, 7.13) * mm, v(10.17, 7.21) * mm, v(10.15, 7.33) * mm, v(10.15, 7.42) * mm, v(10.12, 7.55) * mm, v(10.08, 7.6) * mm, v(10.05, 7.7) * mm, v(10.01, 7.74) * mm, v(9.98, 7.8) * mm, v(9.94, 7.86) * mm, v(9.87, 7.94) * mm, v(9.82, 8) * mm, v(9.74, 8.1) * mm, v(9.7, 8.15) * mm, v(9.66, 8.22) * mm, v(9.6, 8.27) * mm, v(9.5, 8.3) * mm, v(9.29, 8.59) * mm, v(9.18, 8.73) * mm, v(9.15, 8.8) * mm, v(9.07, 8.92) * mm, v(8.98, 9) * mm, v(8.96, 9.08) * mm, v(8.92, 9.14) * mm, v(8.77, 9.46) * mm, v(8.71, 9.6) * mm, v(8.7, 9.68) * mm, v(8.68, 9.78) * mm, v(8.68, 9.9) * mm, v(8.67, 9.97) * mm, v(8.68, 10.04) * mm, v(8.7, 10.1) * mm, v(8.69, 10.17) * mm, v(8.67, 10.35) * mm, v(8.67, 10.46) * mm, v(8.68, 10.6) * mm, v(8.66, 10.7) * mm, v(8.73, 10.84) * mm, v(8.77, 10.98) * mm, v(8.79, 11.04) * mm, v(8.83, 11.13) * mm, v(8.94, 11.16) * mm, v(9.1, 11.25) * mm, v(9.32, 11.32) * mm, v(9.51, 11.3) * mm, v(9.8, 11.28) * mm, v(9.84, 11.26) * mm, v(10.02, 11.2) * mm, v(10.07, 11.17) * mm, v(10.2, 11.12) * mm, v(10.24, 11.07) * mm, v(10.32, 11.02) * mm, v(10.6, 10.67) * mm, v(10.74, 10.58) * mm, v(10.86, 10.43) * mm, v(10.97, 10.18) * mm, v(10.99, 10.12) * mm, v(11.04, 10.07) * mm, v(11.06, 9.83) * mm, v(11.07, 9.75) * mm, v(11.06, 9.64) * mm, v(11.07, 9.57) * mm, v(11.05, 9.48) * mm, v(11.04, 9.41) * mm, v(11, 9.32) * mm, v(11.04, 9.21) * mm, v(11, 9.2) * mm]});
            skFitSpline(sketch, "E139.64", {"points": [v(-0.62, -16.63) * mm, v(-0.7, -16.63) * mm, v(-0.84, -16.63) * mm, v(-0.95, -16.63) * mm, v(-1.14, -16.62) * mm, v(-1.24, -16.64) * mm, v(-1.31, -16.74) * mm, v(-1.33, -16.89) * mm, v(-1.34, -16.98) * mm, v(-1.49, -17.06) * mm, v(-1.64, -17.02) * mm, v(-1.81, -16.93) * mm, v(-1.84, -16.75) * mm, v(-1.78, -16.57) * mm, v(-1.75, -16.44) * mm, v(-1.61, -16.36) * mm, v(-1.52, -16.3) * mm, v(-1.48, -16.27) * mm, v(-1.34, -16.29) * mm, v(-1.23, -16.17) * mm, v(-1.09, -16.2) * mm, v(-0.94, -16.17) * mm, v(-0.7, -16.23) * mm, v(-0.7, -15.92) * mm, v(-0.7, -15.8) * mm, v(-0.72, -15.54) * mm, v(-0.6, -15.33) * mm, v(-0.63, -15.14) * mm, v(-0.55, -14.9) * mm, v(0.34, -14.77) * mm, v(-0.59, -14.65) * mm, v(-0.64, -14.44) * mm, v(-0.89, -14.29) * mm, v(-1.02, -14.1) * mm, v(-1.23, -14.03) * mm, v(-1.32, -14) * mm, v(-1.41, -14.08) * mm, v(-1.46, -14.22) * mm, v(-1.35, -14.36) * mm, v(-1.23, -14.4) * mm, v(-1.15, -14.55) * mm, v(-1.2, -14.68) * mm, v(-1.23, -14.78) * mm, v(-1.34, -14.89) * mm, v(-1.48, -14.9) * mm, v(-1.6, -14.82) * mm, v(-1.78, -14.68) * mm, v(-1.8, -14.4) * mm, v(-1.79, -14.22) * mm, v(-1.72, -13.95) * mm, v(-1.78, -13.8) * mm, v(-1.85, -13.76) * mm, v(-1.98, -13.77) * mm, v(-2.09, -13.87) * mm, v(-2.1, -13.98) * mm, v(-2.15, -14.07) * mm, v(-2.2, -14.15) * mm, v(-2.35, -14.13) * mm, v(-2.4, -14.11) * mm, v(-2.5, -14.08) * mm, v(-2.53, -14) * mm, v(-2.53, -13.89) * mm, v(-2.49, -13.73) * mm, v(-2.42, -13.6) * mm, v(-2.38, -13.55) * mm, v(-2.29, -13.38) * mm, v(-2.16, -13.33) * mm, v(-2, -13.32) * mm, v(-1.93, -13.32) * mm, v(-1.85, -13.29) * mm, v(-1.83, -13.23) * mm, v(-1.79, -13.16) * mm, v(-1.67, -13.12) * mm, v(-1.55, -13.22) * mm, v(-1.46, -13.32) * mm, v(-1.29, -13.37) * mm, v(-1.25, -13.37) * mm, v(-1.13, -13.38) * mm, v(-1.03, -13.28) * mm, v(-0.99, -13.07) * mm, v(-1.07, -12.95) * mm, v(-1.31, -12.93) * mm, v(-1.42, -13) * mm, v(-1.53, -12.91) * mm, v(-1.54, -12.86) * mm, v(-1.6, -12.66) * mm, v(-1.56, -12.46) * mm, v(-1.53, -12.35) * mm, v(-1.5, -12.08) * mm, v(-1.48, -12.05) * mm, v(-1.51, -11.87) * mm, v(-1.65, -11.78) * mm, v(-1.65, -11.74) * mm, v(-1.74, -11.65) * mm, v(-1.74, -11.61) * mm, v(-1.77, -11.55) * mm, v(-1.8, -11.5) * mm, v(-1.85, -11.47) * mm, v(-1.95, -11.3) * mm, v(-1.98, -11.14) * mm, v(-1.8, -11.25) * mm, v(-1.77, -11.3) * mm, v(-1.65, -11.35) * mm, v(-1.6, -11.29) * mm, v(-1.68, -11.17) * mm, v(-1.73, -11.07) * mm, v(-1.75, -10.99) * mm, v(-1.64, -10.95) * mm, v(-1.6, -10.95) * mm, v(-1.47, -11.1) * mm, v(-1.34, -11.15) * mm, v(-1.1, -11.26) * mm, v(-0.95, -11.25) * mm, v(-0.7, -11.33) * mm, v(-0.58, -11.34) * mm, v(-0.42, -11.41) * mm, v(-0.26, -11.43) * mm, v(-0.19, -11.46) * mm, v(-0.1, -11.47) * mm, v(0.22, -11.63) * mm, v(0.43, -11.77) * mm, v(0.48, -11.8) * mm, v(0.54, -11.9) * mm, v(0.58, -11.93) * mm, v(0.64, -12) * mm, v(0.68, -12.14) * mm, v(0.73, -12.18) * mm, v(0.77, -12.34) * mm, v(0.98, -12.85) * mm, v(1.03, -13.1) * mm, v(1.15, -13.66) * mm, v(1.22, -13.9) * mm, v(1.21, -14.1) * mm, v(1.22, -14.25) * mm, v(1.32, -14.65) * mm, v(1.4, -14.82) * mm, v(1.47, -14.98) * mm, v(1.52, -15.06) * mm, v(1.64, -15.08) * mm, v(1.68, -15.08) * mm, v(1.75, -15.1) * mm, v(1.88, -15) * mm, v(1.86, -14.94) * mm, v(1.87, -14.8) * mm, v(1.8, -14.69) * mm, v(1.78, -14.64) * mm, v(1.75, -14.57) * mm, v(1.7, -14.38) * mm, v(1.67, -14.34) * mm, v(1.63, -14.24) * mm, v(1.61, -14.2) * mm, v(1.48, -13.87) * mm, v(1.5, -13.79) * mm, v(1.43, -13.6) * mm, v(1.44, -13.5) * mm, v(1.4, -13.3) * mm, v(1.42, -13.23) * mm, v(1.42, -13.15) * mm, v(1.44, -13.08) * mm, v(1.45, -13.04) * mm, v(1.54, -12.82) * mm, v(1.64, -12.8) * mm, v(1.72, -12.75) * mm, v(1.87, -12.77) * mm, v(1.97, -12.79) * mm, v(2.07, -12.84) * mm, v(2.12, -12.91) * mm, v(2.43, -12.98) * mm, v(2.42, -12.97) * mm, v(2.42, -12.97) * mm]});
            skArc(sketch, "E140.0", {"start": v(-3.75, -11.16) * mm, "mid": v(-3.57, -10.57) * mm, "end": v(-3.06, -10.2) * mm});
            skFitSpline(sketch, "E141.0", {"points": [v(2.15, -12.9) * mm, v(2.24, -12.97) * mm, v(2.45, -13.14) * mm, v(2.54, -14.14) * mm, v(2.02, -13.79) * mm, v(1.98, -13.58) * mm, v(1.92, -13.4) * mm, v(1.99, -13.25) * mm, v(1.83, -13.12) * mm, v(1.77, -13.26) * mm, v(1.74, -13.35) * mm, v(1.75, -13.51) * mm, v(1.8, -13.68) * mm, v(1.9, -13.87) * mm, v(1.98, -14.07) * mm, v(2.08, -14.32) * mm, v(2.18, -14.53) * mm, v(2.2, -14.85) * mm, v(2.2, -14.95) * mm, v(2.3, -15.31) * mm, v(2.25, -15.56) * mm, v(2.12, -15.75) * mm, v(2.01, -15.92) * mm, v(1.99, -16.15) * mm, v(1.77, -16.38) * mm, v(1.74, -16.44) * mm, v(1.58, -16.72) * mm, v(1.5, -16.78) * mm, v(1.46, -16.97) * mm, v(1.5, -17.1) * mm, v(1.5, -17.2) * mm, v(1.68, -17.35) * mm, v(1.5, -17.52) * mm, v(1.3, -17.73) * mm, v(1.16, -17.95) * mm, v(1.11, -18.13) * mm, v(1.1, -18.3) * mm, v(1.3, -18.38) * mm, v(1.15, -18.68) * mm, v(1.03, -18.71) * mm, v(0.87, -18.75) * mm, v(0.68, -18.71) * mm, v(0.65, -18.63) * mm, v(0.62, -18.58) * mm, v(0.59, -18.5) * mm, v(0.57, -18.32) * mm, v(0.58, -18.14) * mm, v(0.62, -18.04) * mm, v(0.61, -17.96) * mm, v(0.61, -17.87) * mm, v(0.68, -17.78) * mm, v(0.77, -17.81) * mm, v(0.85, -17.76) * mm, v(0.82, -17.53) * mm, v(0.84, -17.33) * mm, v(0.74, -17.15) * mm, v(0.68, -17.06) * mm, v(0.65, -16.97) * mm, v(0.53, -16.77) * mm, v(0.44, -16.71) * mm, v(0.34, -16.52) * mm, v(0.27, -16.46) * mm, v(0.11, -16.32) * mm, v(0, -16.4) * mm, v(-0.14, -16.42) * mm, v(-0.26, -16.65) * mm, v(-0.37, -16.62) * mm, v(-0.61, -16.63) * mm, v(-0.62, -16.63) * mm, v(-0.63, -16.63) * mm]});
            skFitSpline(sketch, "E141.1", {"points": [v(-0.62, -16.63) * mm, v(-0.7, -16.63) * mm, v(-0.84, -16.63) * mm, v(-0.95, -16.63) * mm, v(-1.14, -16.62) * mm, v(-1.24, -16.64) * mm, v(-1.31, -16.74) * mm, v(-1.33, -16.89) * mm, v(-1.34, -16.98) * mm, v(-1.49, -17.06) * mm, v(-1.64, -17.02) * mm, v(-1.81, -16.93) * mm, v(-1.84, -16.75) * mm, v(-1.78, -16.57) * mm, v(-1.75, -16.44) * mm, v(-1.61, -16.36) * mm, v(-1.52, -16.3) * mm, v(-1.48, -16.27) * mm, v(-1.34, -16.29) * mm, v(-1.23, -16.17) * mm, v(-1.09, -16.2) * mm, v(-0.94, -16.17) * mm, v(-0.7, -16.23) * mm, v(-0.7, -15.92) * mm, v(-0.7, -15.8) * mm, v(-0.72, -15.54) * mm, v(-0.6, -15.33) * mm, v(-0.63, -15.14) * mm, v(-0.55, -14.9) * mm, v(0.34, -14.77) * mm, v(-0.59, -14.65) * mm, v(-0.64, -14.44) * mm, v(-0.89, -14.29) * mm, v(-1.02, -14.1) * mm, v(-1.23, -14.03) * mm, v(-1.32, -14) * mm, v(-1.41, -14.08) * mm, v(-1.46, -14.22) * mm, v(-1.35, -14.36) * mm, v(-1.23, -14.4) * mm, v(-1.15, -14.55) * mm, v(-1.2, -14.68) * mm, v(-1.23, -14.78) * mm, v(-1.34, -14.89) * mm, v(-1.48, -14.9) * mm, v(-1.6, -14.82) * mm, v(-1.78, -14.68) * mm, v(-1.8, -14.4) * mm, v(-1.79, -14.22) * mm, v(-1.72, -13.95) * mm, v(-1.78, -13.8) * mm, v(-1.85, -13.76) * mm, v(-1.98, -13.77) * mm, v(-2.09, -13.87) * mm, v(-2.1, -13.98) * mm, v(-2.15, -14.07) * mm, v(-2.2, -14.15) * mm, v(-2.35, -14.13) * mm, v(-2.4, -14.11) * mm, v(-2.5, -14.08) * mm, v(-2.53, -14) * mm, v(-2.53, -13.89) * mm, v(-2.49, -13.73) * mm, v(-2.42, -13.6) * mm, v(-2.38, -13.55) * mm, v(-2.29, -13.38) * mm, v(-2.16, -13.33) * mm, v(-2, -13.32) * mm, v(-1.93, -13.32) * mm, v(-1.85, -13.29) * mm, v(-1.83, -13.23) * mm, v(-1.79, -13.16) * mm, v(-1.67, -13.12) * mm, v(-1.55, -13.22) * mm, v(-1.46, -13.32) * mm, v(-1.29, -13.37) * mm, v(-1.25, -13.37) * mm, v(-1.13, -13.38) * mm, v(-1.03, -13.28) * mm, v(-0.99, -13.07) * mm, v(-1.07, -12.95) * mm, v(-1.31, -12.93) * mm, v(-1.42, -13) * mm, v(-1.53, -12.91) * mm, v(-1.54, -12.86) * mm, v(-1.6, -12.66) * mm, v(-1.56, -12.46) * mm, v(-1.53, -12.35) * mm, v(-1.5, -12.08) * mm, v(-1.48, -12.05) * mm, v(-1.51, -11.87) * mm, v(-1.65, -11.78) * mm, v(-1.65, -11.74) * mm, v(-1.74, -11.65) * mm, v(-1.74, -11.61) * mm, v(-1.77, -11.55) * mm, v(-1.8, -11.5) * mm, v(-1.85, -11.47) * mm, v(-1.95, -11.3) * mm, v(-1.98, -11.14) * mm, v(-1.8, -11.25) * mm, v(-1.77, -11.3) * mm, v(-1.65, -11.35) * mm, v(-1.6, -11.29) * mm, v(-1.68, -11.17) * mm, v(-1.73, -11.07) * mm, v(-1.75, -10.99) * mm, v(-1.64, -10.95) * mm, v(-1.6, -10.95) * mm, v(-1.47, -11.1) * mm, v(-1.34, -11.15) * mm, v(-1.1, -11.26) * mm, v(-0.95, -11.25) * mm, v(-0.7, -11.33) * mm, v(-0.58, -11.34) * mm, v(-0.42, -11.41) * mm, v(-0.26, -11.43) * mm, v(-0.19, -11.46) * mm, v(-0.1, -11.47) * mm, v(0.22, -11.63) * mm, v(0.43, -11.77) * mm, v(0.48, -11.8) * mm, v(0.54, -11.9) * mm, v(0.58, -11.93) * mm, v(0.64, -12) * mm, v(0.68, -12.14) * mm, v(0.73, -12.18) * mm, v(0.77, -12.34) * mm, v(0.98, -12.85) * mm, v(1.03, -13.1) * mm, v(1.15, -13.66) * mm, v(1.22, -13.9) * mm, v(1.21, -14.1) * mm, v(1.22, -14.25) * mm, v(1.32, -14.65) * mm, v(1.4, -14.82) * mm, v(1.47, -14.98) * mm, v(1.52, -15.06) * mm, v(1.64, -15.08) * mm, v(1.68, -15.08) * mm, v(1.75, -15.1) * mm, v(1.88, -15) * mm, v(1.86, -14.94) * mm, v(1.87, -14.8) * mm, v(1.8, -14.69) * mm, v(1.78, -14.64) * mm, v(1.75, -14.57) * mm, v(1.7, -14.38) * mm, v(1.67, -14.34) * mm, v(1.63, -14.24) * mm, v(1.61, -14.2) * mm, v(1.48, -13.87) * mm, v(1.5, -13.79) * mm, v(1.43, -13.6) * mm, v(1.44, -13.5) * mm, v(1.4, -13.3) * mm, v(1.42, -13.23) * mm, v(1.42, -13.15) * mm, v(1.44, -13.08) * mm, v(1.45, -13.04) * mm, v(1.54, -12.82) * mm, v(1.64, -12.8) * mm, v(1.72, -12.75) * mm, v(1.87, -12.77) * mm, v(1.97, -12.79) * mm, v(2.07, -12.84) * mm, v(2.12, -12.91) * mm, v(2.43, -12.98) * mm, v(2.42, -12.97) * mm, v(2.42, -12.97) * mm]});
            skLineSegment(sketch, "E142.0", {"start": v(-1.54, -6.32) * mm, "end": v(-1.2, -5.88) * mm});
            skLineSegment(sketch, "E142.1", {"start": v(2.23, -7.36) * mm, "end": v(1.8, -7.36) * mm});
            skLineSegment(sketch, "E142.2", {"start": v(3.28, -7.14) * mm, "end": v(3.2, -6.62) * mm});
            skLineSegment(sketch, "E142.3", {"start": v(-2.23, -7.36) * mm, "end": v(-1.8, -7.36) * mm});
            skLineSegment(sketch, "E142.4", {"start": v(-2.76, -6.8) * mm, "end": v(-2.23, -7.36) * mm});
            skLineSegment(sketch, "E142.5", {"start": v(2.76, -6.8) * mm, "end": v(2.23, -7.36) * mm});
            skLineSegment(sketch, "E142.6", {"start": v(0.72, -6.24) * mm, "end": v(0.67, -6.78) * mm});
            skLineSegment(sketch, "E142.7", {"start": v(-3.2, -6.62) * mm, "end": v(-2.76, -6.8) * mm});
            skLineSegment(sketch, "E142.8", {"start": v(1.44, -7.04) * mm, "end": v(1.54, -6.32) * mm});
            skLineSegment(sketch, "E142.9", {"start": v(-2.34, -8.82) * mm, "end": v(-3.28, -7.14) * mm});
            skLineSegment(sketch, "E142.10", {"start": v(1.54, -6.32) * mm, "end": v(1.2, -5.88) * mm});
            skLineSegment(sketch, "E142.11", {"start": v(1.2, -5.88) * mm, "end": v(0.72, -6.24) * mm});
            skLineSegment(sketch, "E142.12", {"start": v(-3.28, -7.14) * mm, "end": v(-3.2, -6.62) * mm});
            skLineSegment(sketch, "E142.13", {"start": v(0, -8.36) * mm, "end": v(0, -5.24) * mm});
            skLineSegment(sketch, "E142.14", {"start": v(2.34, -8.82) * mm, "end": v(3.28, -7.14) * mm});
            skLineSegment(sketch, "E142.15", {"start": v(-1.2, -5.88) * mm, "end": v(-0.72, -6.24) * mm});
            skLineSegment(sketch, "E142.16", {"start": v(-1.44, -7.04) * mm, "end": v(-1.54, -6.32) * mm});
            skLineSegment(sketch, "E142.17", {"start": v(-0.72, -6.24) * mm, "end": v(-0.67, -6.78) * mm});
            skLineSegment(sketch, "E142.18", {"start": v(3.2, -6.62) * mm, "end": v(2.76, -6.8) * mm});
            skFitSpline(sketch, "E143.0", {"points": [v(11, 9.2) * mm, v(10.87, 9.15) * mm, v(10, 9.5) * mm, v(10.13, 9.69) * mm, v(10.1, 9.76) * mm, v(10.13, 9.94) * mm, v(10.13, 10.05) * mm, v(10.08, 10.2) * mm, v(10.07, 10.32) * mm, v(9.99, 10.4) * mm, v(9.94, 10.46) * mm, v(9.83, 10.52) * mm, v(9.68, 10.5) * mm, v(9.57, 10.39) * mm, v(9.57, 10.22) * mm, v(9.55, 10.1) * mm, v(9.54, 9.85) * mm, v(9.53, 9.78) * mm, v(9.54, 9.67) * mm, v(9.56, 9.62) * mm, v(9.6, 9.5) * mm, v(9.63, 9.46) * mm, v(9.7, 9.35) * mm, v(9.72, 9.3) * mm, v(9.78, 9.22) * mm, v(9.81, 9.17) * mm, v(9.91, 9.08) * mm, v(10.02, 8.98) * mm, v(10.05, 8.93) * mm, v(10.1, 8.87) * mm, v(10.16, 8.8) * mm, v(10.24, 8.72) * mm, v(10.41, 8.6) * mm, v(10.56, 8.41) * mm, v(10.68, 8.26) * mm, v(10.71, 8.19) * mm, v(10.81, 8.08) * mm, v(10.85, 7.98) * mm, v(10.95, 7.84) * mm, v(10.97, 7.76) * mm, v(11.04, 7.63) * mm, v(11.09, 7.49) * mm, v(11.1, 7.44) * mm, v(11.11, 7.07) * mm, v(11.11, 6.9) * mm, v(11.1, 6.8) * mm, v(11.09, 6.66) * mm, v(11.08, 6.59) * mm, v(11.08, 6.43) * mm, v(11.05, 6.37) * mm, v(11.05, 6.24) * mm, v(11.01, 6.16) * mm, v(11.01, 6.07) * mm, v(10.94, 5.92) * mm, v(10.86, 5.85) * mm, v(10.72, 5.82) * mm, v(10.54, 5.79) * mm, v(10.42, 5.8) * mm, v(10.23, 5.8) * mm, v(10.15, 5.81) * mm, v(9.93, 5.87) * mm, v(9.78, 5.94) * mm, v(9.48, 6.04) * mm, v(9.4, 6.13) * mm, v(9.32, 6.2) * mm, v(9.23, 6.3) * mm, v(9.14, 6.34) * mm, v(9.1, 6.39) * mm, v(9.04, 6.47) * mm, v(9, 6.53) * mm, v(8.9, 6.66) * mm, v(8.87, 6.72) * mm, v(8.82, 6.79) * mm, v(8.8, 6.83) * mm, v(8.75, 6.94) * mm, v(8.74, 7) * mm, v(8.69, 7.07) * mm, v(8.66, 7.19) * mm, v(8.67, 7.26) * mm, v(8.66, 7.52) * mm, v(8.72, 7.83) * mm, v(8.71, 7.9) * mm, v(8.76, 8.04) * mm, v(8.9, 7.98) * mm, v(9.02, 7.95) * mm, v(9.19, 7.9) * mm, v(9.25, 7.86) * mm, v(9.35, 7.8) * mm, v(9.48, 7.78) * mm, v(9.56, 7.72) * mm, v(9.6, 7.64) * mm, v(9.63, 7.59) * mm, v(9.65, 7.48) * mm, v(9.64, 7.4) * mm, v(9.65, 7.28) * mm, v(9.62, 7.2) * mm, v(9.63, 7.11) * mm, v(9.62, 7.05) * mm, v(9.63, 6.96) * mm, v(9.62, 6.9) * mm, v(9.66, 6.83) * mm, v(9.68, 6.73) * mm, v(9.75, 6.64) * mm, v(9.8, 6.56) * mm, v(9.88, 6.55) * mm, v(10, 6.56) * mm, v(10.12, 6.68) * mm, v(10.15, 6.78) * mm, v(10.18, 6.83) * mm, v(10.19, 6.94) * mm, v(10.2, 7.01) * mm, v(10.16, 7.13) * mm, v(10.17, 7.21) * mm, v(10.15, 7.33) * mm, v(10.15, 7.42) * mm, v(10.12, 7.55) * mm, v(10.08, 7.6) * mm, v(10.05, 7.7) * mm, v(10.01, 7.74) * mm, v(9.98, 7.8) * mm, v(9.94, 7.86) * mm, v(9.87, 7.94) * mm, v(9.82, 8) * mm, v(9.74, 8.1) * mm, v(9.7, 8.15) * mm, v(9.66, 8.22) * mm, v(9.6, 8.27) * mm, v(9.5, 8.3) * mm, v(9.29, 8.59) * mm, v(9.18, 8.73) * mm, v(9.15, 8.8) * mm, v(9.07, 8.92) * mm, v(8.98, 9) * mm, v(8.96, 9.08) * mm, v(8.92, 9.14) * mm, v(8.77, 9.46) * mm, v(8.71, 9.6) * mm, v(8.7, 9.68) * mm, v(8.68, 9.78) * mm, v(8.68, 9.9) * mm, v(8.67, 9.97) * mm, v(8.68, 10.04) * mm, v(8.7, 10.1) * mm, v(8.69, 10.17) * mm, v(8.67, 10.35) * mm, v(8.67, 10.46) * mm, v(8.68, 10.6) * mm, v(8.66, 10.7) * mm, v(8.73, 10.84) * mm, v(8.77, 10.98) * mm, v(8.79, 11.04) * mm, v(8.83, 11.13) * mm, v(8.94, 11.16) * mm, v(9.1, 11.25) * mm, v(9.32, 11.32) * mm, v(9.51, 11.3) * mm, v(9.8, 11.28) * mm, v(9.84, 11.26) * mm, v(10.02, 11.2) * mm, v(10.07, 11.17) * mm, v(10.2, 11.12) * mm, v(10.24, 11.07) * mm, v(10.32, 11.02) * mm, v(10.6, 10.67) * mm, v(10.74, 10.58) * mm, v(10.86, 10.43) * mm, v(10.97, 10.18) * mm, v(10.99, 10.12) * mm, v(11.04, 10.07) * mm, v(11.06, 9.83) * mm, v(11.07, 9.75) * mm, v(11.06, 9.64) * mm, v(11.07, 9.57) * mm, v(11.05, 9.48) * mm, v(11.04, 9.41) * mm, v(11, 9.32) * mm, v(11.04, 9.21) * mm, v(11, 9.2) * mm]});
            skArc(sketch, "E144.0", {"start": v(8.14, 11.68) * mm, "mid": v(7.62, 11.83) * mm, "end": v(7.1, 11.98) * mm});
            skLineSegment(sketch, "E144.1", {"start": v(5.54, 12.34) * mm, "end": v(6.6, 12.1) * mm});
            skFitSpline(sketch, "E144.2", {"points": [v(8.14, 7.6) * mm, v(8.14, 7.47) * mm, v(8.13, 7.21) * mm, v(7.82, 6.95) * mm, v(7.53, 6.76) * mm, v(7.13, 6.8) * mm, v(6.6, 6.88) * mm, v(6.22, 7.1) * mm, v(6, 7.28) * mm, v(5.75, 7.6) * mm, v(5.63, 7.92) * mm, v(5.57, 8.1) * mm, v(5.54, 8.18) * mm]});
            skLineSegment(sketch, "E144.3", {"start": v(8.14, 11.68) * mm, "end": v(8.14, 7.6) * mm});
            skFitSpline(sketch, "E144.4", {"points": [v(7.1, 7.96) * mm, v(7.1, 7.89) * mm, v(7.1, 7.75) * mm, v(7.07, 7.58) * mm, v(6.83, 7.55) * mm, v(6.8, 7.54) * mm, v(6.66, 7.59) * mm, v(6.54, 7.73) * mm, v(6.57, 7.95) * mm, v(6.59, 8.01) * mm, v(6.6, 8.03) * mm]});
            skLineSegment(sketch, "E145.0", {"start": v(2.62, 11.93) * mm, "end": v(3.33, 11.8) * mm});
            skArc(sketch, "E145.1", {"start": v(4.43, 7.35) * mm, "mid": v(3.88, 7.43) * mm, "end": v(3.33, 7.5) * mm});
            skLineSegment(sketch, "E145.2", {"start": v(5.1, 11.4) * mm, "end": v(4.43, 11.57) * mm});
            skLineSegment(sketch, "E145.3", {"start": v(2.62, 12.78) * mm, "end": v(2.62, 11.93) * mm});
            skLineSegment(sketch, "E146.0", {"start": v(5.1, 12.43) * mm, "end": v(5.1, 11.4) * mm});
            skArc(sketch, "E147.0", {"start": v(2.17, 12.82) * mm, "mid": v(1.76, 12.85) * mm, "end": v(1.35, 12.87) * mm});
            skArc(sketch, "E148.0", {"start": v(0.45, 12.9) * mm, "mid": v(0.05, 12.9) * mm, "end": v(-0.35, 12.9) * mm});
            skArc(sketch, "E149.0", {"start": v(0.45, 7.7) * mm, "mid": v(0.05, 7.7) * mm, "end": v(-0.35, 7.7) * mm});
            skLineSegment(sketch, "E150.0", {"start": v(-0.35, 12.9) * mm, "end": v(-0.35, 7.7) * mm});
            skArc(sketch, "E151.0", {"start": v(2.17, 7.62) * mm, "mid": v(1.73, 7.65) * mm, "end": v(1.28, 7.68) * mm});
            skLineSegment(sketch, "E152.0", {"start": v(-0.97, 11.95) * mm, "end": v(-1.77, 11.95) * mm});
            skLineSegment(sketch, "E152.1", {"start": v(-1.77, 10.76) * mm, "end": v(-1.02, 10.76) * mm});
            skLineSegment(sketch, "E152.3", {"start": v(-1.77, 11.95) * mm, "end": v(-1.77, 10.76) * mm});
            skLineSegment(sketch, "E152.5", {"start": v(-1.02, 9.87) * mm, "end": v(-1.77, 9.87) * mm});
            skLineSegment(sketch, "E152.6", {"start": v(-0.97, 12.89) * mm, "end": v(-0.97, 11.95) * mm});
            skLineSegment(sketch, "E152.7", {"start": v(-1.02, 10.76) * mm, "end": v(-1.02, 9.87) * mm});
            skLineSegment(sketch, "E152.8", {"start": v(-1.77, 9.87) * mm, "end": v(-1.77, 8.6) * mm});
            skLineSegment(sketch, "E152.9", {"start": v(-0.86, 8.6) * mm, "end": v(-0.86, 7.7) * mm});
            skLineSegment(sketch, "E152.10", {"start": v(-1.77, 8.6) * mm, "end": v(-0.86, 8.6) * mm});
            skArc(sketch, "E153.0", {"start": v(-3.2, 12.72) * mm, "mid": v(-3.75, 12.65) * mm, "end": v(-4.3, 12.57) * mm});
            skArc(sketch, "E154.0", {"start": v(-3.8, 7.45) * mm, "mid": v(-4.65, 7.31) * mm, "end": v(-5.5, 7.16) * mm});
            skArc(sketch, "E155.0", {"start": v(-5.13, 12.43) * mm, "mid": v(-5.65, 12.32) * mm, "end": v(-6.17, 12.2) * mm});
            skArc(sketch, "E156.0", {"start": v(-6.52, 12.12) * mm, "mid": v(-7.06, 11.99) * mm, "end": v(-7.6, 11.84) * mm});
            skArc(sketch, "E157.0", {"start": v(-8.07, 11.7) * mm, "mid": v(-8.62, 11.53) * mm, "end": v(-9.17, 11.34) * mm});
            skArc(sketch, "E158.0", {"start": v(-9.68, 11.16) * mm, "mid": v(-10.2, 10.95) * mm, "end": v(-10.74, 10.74) * mm});
            skArc(sketch, "E159.0", {"start": v(-7.88, 6.57) * mm, "mid": v(-8.05, 6.52) * mm, "end": v(-8.2, 6.47) * mm});
            skFitSpline(sketch, "E159.1", {"points": [v(-9.17, 7.24) * mm, v(-9.15, 7.12) * mm, v(-9.13, 6.91) * mm, v(-9.03, 6.75) * mm, v(-8.84, 6.58) * mm, v(-8.38, 6.38) * mm, v(-7.9, 6.58) * mm, v(-7.25, 6.73) * mm, v(-7.03, 6.98) * mm, v(-6.81, 7.3) * mm, v(-6.6, 7.6) * mm, v(-6.54, 7.67) * mm, v(-6.52, 7.7) * mm]});
            skFitSpline(sketch, "E159.6", {"points": [v(-7.6, 7.62) * mm, v(-7.6, 7.57) * mm, v(-7.58, 7.47) * mm, v(-7.66, 7.35) * mm, v(-7.85, 7.2) * mm, v(-8.07, 7.3) * mm, v(-8.07, 7.43) * mm, v(-8.07, 7.5) * mm]});
            skArc(sketch, "E160.0", {"start": v(-10.51, 5.64) * mm, "mid": v(-10.86, 5.5) * mm, "end": v(-11.2, 5.36) * mm});
            skFitSpline(sketch, "E160.1", {"points": [v(-9.68, 6.66) * mm, v(-9.7, 6.6) * mm, v(-9.74, 6.48) * mm, v(-9.9, 6.22) * mm, v(-9.98, 6.07) * mm, v(-10.26, 5.87) * mm, v(-10.4, 5.74) * mm, v(-10.5, 5.63) * mm, v(-10.65, 5.58) * mm, v(-10.73, 5.55) * mm]});
            skFitSpline(sketch, "E160.2", {"points": [v(-11.2, 5.36) * mm, v(-11.18, 5.43) * mm, v(-11.12, 5.6) * mm, v(-11.25, 6.19) * mm, v(-10.96, 6.25) * mm, v(-10.88, 6.3) * mm, v(-10.78, 6.42) * mm, v(-10.75, 6.5) * mm, v(-10.73, 6.6) * mm, v(-10.74, 6.83) * mm, v(-10.74, 6.99) * mm]});
            skLineSegment(sketch, "E161.0", {"start": v(1.8, -7.36) * mm, "end": v(1.44, -7.04) * mm});
            skLineSegment(sketch, "E162.0", {"start": v(0.67, -6.78) * mm, "end": v(0.31, -7.14) * mm});
            skPoint(sketch, "E163.0", {"position": v(0.16, -7.14) * mm});
            skLineSegment(sketch, "E164.0", {"start": v(-1.8, -7.36) * mm, "end": v(-1.44, -7.04) * mm});
            skLineSegment(sketch, "E165.0", {"start": v(-0.31, -7.14) * mm, "end": v(0, -7.14) * mm});
            skLineSegment(sketch, "E165.1", {"start": v(-0.67, -6.78) * mm, "end": v(-0.31, -7.14) * mm});
            skLineSegment(sketch, "E166.0", {"start": v(0.31, -7.14) * mm, "end": v(0, -7.14) * mm});
            skArc(sketch, "E167.0", {"start": v(3.75, -11.16) * mm, "mid": v(3.57, -10.57) * mm, "end": v(3.06, -10.2) * mm});
            const initialGuessF3  = {"E139.30": [0, 0, 0, 1, 0.022562885147601155, 0.012851271823588573, 0.502769524575932, 1.0162238153190999], "E139.35": [0, 0, 0, 1, 0.022562885147601155, 0.012851271823588573, 6.094011800529932, 0.19398440980100334], "E139.38": [0, 0, 0, -1, 0.020476011405082317, 0.01260289410030643, 5.220938072999507, 5.783566470268216], "E139.47": [0, 0, 0, 1, 0.022562885147601155, 0.012851271823588573, 4.722050642778372, 4.867301040875056], "E139.51": [0, 0, 0, 1, 0.022562885147601155, 0.012851271823588573, 5.266961491860487, 5.806421527511528], "E139.55": [0, 0, 0, 1, 0.022562885147601155, 0.012851271823588573, 1.4158842663045312, 1.5611346644012138], "E139.56": [0, 0, 0, -1, 0.020476011405082317, 0.01260289410030643, 0.499924631436077, 1.0622472341800782]};
            skSetInitialGuess(sketch, initialGuessF3);
            skSolve(sketch);
        }
        {
            var Q0;
            Q0 = qSketchRegion(id + "F3", true);
            extrude(context, id + "F4", {"entities" : qUnion([Q0]), "operationType" : NewBodyOperationType.ADD, "depth" : 0.5 * mm});
        }
        {
            var Q0;
            Q0=makeQuery(id+"F3.imprint","IMPRINT",FACE,{"disambiguationData":[TD([[makeQuery(id+"F3.imprint","IMPRINT",EDGE,{"derivedFrom":sQuery(id+"F3.wireOp",EDGE,"E139.12")}),1.0]])]});
            var Q1;
            Q1=makeQuery(id+"F3.imprint","IMPRINT",FACE,{"disambiguationData":[TD([[makeQuery(id+"F3.imprint","IMPRINT",EDGE,{"derivedFrom":sQuery(id+"F3.wireOp",EDGE,"E139.14")}),-1.0]])]});
            var Q2;
            Q2=makeQuery(id+"F3.imprint","IMPRINT",FACE,{"disambiguationData":[TD([[makeQuery(id+"F3.imprint","IMPRINT",EDGE,{"derivedFrom":sQuery(id+"F3.wireOp",EDGE,"E139.0")}),1.0]])]});
            var Q3;
            Q3=makeQuery(id+"F3.imprint","IMPRINT",FACE,{"disambiguationData":[TD([[makeQuery(id+"F3.imprint","IMPRINT",EDGE,{"derivedFrom":sQuery(id+"F3.wireOp",EDGE,"E139.9")}),-1.0]])]});
            var Q4;
            Q4=makeQuery(id+"F3.imprint","IMPRINT",FACE,{"disambiguationData":[TD([[makeQuery(id+"F3.imprint","IMPRINT",EDGE,{"derivedFrom":sQuery(id+"F3.wireOp",EDGE,"E142.1")}),1.0]])]});
            var Q5;
            Q5=makeQuery(id+"F3.imprint","IMPRINT",FACE,{"disambiguationData":[TD([[makeQuery(id+"F3.imprint","IMPRINT",EDGE,{"derivedFrom":sQuery(id+"F3.wireOp",EDGE,"E142.0")}),-1.0]])]});
            var Q6;
            Q6=makeQuery(id+"F3.imprint","IMPRINT",FACE,{"disambiguationData":[TD([[makeQuery(id+"F3.imprint","IMPRINT",EDGE,{"derivedFrom":sQuery(id+"F3.wireOp",EDGE,"E139.45")}),1.0]])]});
            var Q7;
            Q7=makeQuery(id+"F3.imprint","IMPRINT",FACE,{"disambiguationData":[TD([[makeQuery(id+"F3.imprint","IMPRINT",EDGE,{"derivedFrom":sQuery(id+"F3.wireOp",EDGE,"E143.0")}),-1.0]])]});
            var Q8;
            Q8=makeQuery(id+"F3.imprint","IMPRINT",FACE,{"disambiguationData":[TD([[makeQuery(id+"F3.imprint","IMPRINT",EDGE,{"derivedFrom":sQuery(id+"F3.wireOp",EDGE,"E144.0")}),1.0]])]});
            var Q9;
            Q9=makeQuery(id+"F3.imprint","IMPRINT",FACE,{"disambiguationData":[TD([[makeQuery(id+"F3.imprint","IMPRINT",EDGE,{"derivedFrom":sQuery(id+"F3.wireOp",EDGE,"E145.0")}),1.0]])]});
            var Q10;
            Q10=makeQuery(id+"F3.imprint","IMPRINT",FACE,{"disambiguationData":[TD([[makeQuery(id+"F3.imprint","IMPRINT",EDGE,{"derivedFrom":sQuery(id+"F3.wireOp",EDGE,"E139.2")}),1.0]])]});
            var Q11;
            Q11=makeQuery(id+"F3.imprint","IMPRINT",FACE,{"disambiguationData":[TD([[makeQuery(id+"F3.imprint","IMPRINT",EDGE,{"derivedFrom":sQuery(id+"F3.wireOp",EDGE,"E152.0")}),-1.0]])]});
            var Q12;
            Q12=makeQuery(id+"F3.imprint","IMPRINT",FACE,{"disambiguationData":[TD([[makeQuery(id+"F3.imprint","IMPRINT",EDGE,{"derivedFrom":sQuery(id+"F3.wireOp",EDGE,"E139.8")}),1.0]])]});
            var Q13;
            Q13=makeQuery(id+"F3.imprint","IMPRINT",FACE,{"disambiguationData":[TD([[makeQuery(id+"F3.imprint","IMPRINT",EDGE,{"derivedFrom":sQuery(id+"F3.wireOp",EDGE,"E156.0")}),1.0]])]});
            var Q14;
            {var subQ7=sQuery(id+"F3.wireOp",EDGE,"E158.0");Q14=makeQuery(id+"F3.imprint","IMPRINT",FACE,{"disambiguationData":[TD([[makeQuery(id+"F3.imprint","IMPRINT",EDGE,{"derivedFrom":subQ7}),1.0]])]});}
            var Q15;
            Q15=makeQuery(id+"F3.imprint","IMPRINT",FACE,{"disambiguationData":[TD([[makeQuery(id+"F3.imprint","IMPRINT",EDGE,{"derivedFrom":sQuery(id+"F3.wireOp",EDGE,"E139.25")}),-1.0]])]});
            var Q16;
            Q16=makeQuery(id+"F3.imprint","IMPRINT",FACE,{"disambiguationData":[TD([[makeQuery(id+"F3.imprint","IMPRINT",EDGE,{"derivedFrom":sQuery(id+"F3.wireOp",EDGE,"E139.23")}),-1.0]])]});
            var Q17;
            Q17=makeQuery(id+"F3.imprint","IMPRINT",FACE,{"disambiguationData":[TD([[makeQuery(id+"F3.imprint","IMPRINT",EDGE,{"derivedFrom":sQuery(id+"F3.wireOp",EDGE,"E139.5")}),-1.0]])]});
            extrude(context, id + "F5", {"entities" : qUnion([Q0, Q1, Q2, Q3, Q4, Q5, Q6, Q7, Q8, Q9, Q10, Q11, Q12, Q13, Q14, Q15, Q16, Q17]), "operationType" : NewBodyOperationType.ADD, "depth" : 0.5 * mm});
        }
        {
            var Q0;
            Q0=makeQuery(id+"F5.opExtrude","CAP_FACE",FACE,{"disambiguationData":[OSD([sQuery(id+"F3.wireOp",EDGE,"E139.9"),sQuery(id+"F3.wireOp",EDGE,"E139.19"),sQuery(id+"F3.wireOp",EDGE,"E139.36"),sQuery(id+"F3.wireOp",EDGE,"E139.50"),sQuery(id+"F3.wireOp",EDGE,"E139.53"),sQuery(id+"F3.wireOp",EDGE,"E139.57"),sQuery(id+"F3.wireOp",EDGE,"E140.0"),sQuery(id+"F3.wireOp",EDGE,"E141.0"),sQuery(id+"F3.wireOp",EDGE,"E141.1"),sQuery(id+"F3.wireOp",EDGE,"E167.0")])],"isStart":false});
            var sketch = newSketch(context, id + "F6", { "sketchPlane" : qUnion([Q0])});
            skFitSpline(sketch, "E168.0", {"points": [v(2.15, -12.9) * mm, v(2.24, -12.97) * mm, v(2.45, -13.14) * mm, v(2.54, -14.14) * mm, v(2.02, -13.79) * mm, v(1.98, -13.58) * mm, v(1.92, -13.4) * mm, v(1.99, -13.25) * mm, v(1.83, -13.12) * mm, v(1.77, -13.26) * mm, v(1.74, -13.35) * mm, v(1.75, -13.51) * mm, v(1.8, -13.68) * mm, v(1.9, -13.87) * mm, v(1.98, -14.07) * mm, v(2.08, -14.32) * mm, v(2.18, -14.53) * mm, v(2.2, -14.85) * mm, v(2.2, -14.95) * mm, v(2.3, -15.31) * mm, v(2.25, -15.56) * mm, v(2.12, -15.75) * mm, v(2.01, -15.92) * mm, v(1.99, -16.15) * mm, v(1.77, -16.38) * mm, v(1.74, -16.44) * mm, v(1.58, -16.72) * mm, v(1.5, -16.78) * mm, v(1.46, -16.97) * mm, v(1.5, -17.1) * mm, v(1.5, -17.2) * mm, v(1.68, -17.35) * mm, v(1.5, -17.52) * mm, v(1.3, -17.73) * mm, v(1.16, -17.95) * mm, v(1.11, -18.13) * mm, v(1.1, -18.3) * mm, v(1.3, -18.38) * mm, v(1.15, -18.68) * mm, v(1.03, -18.71) * mm, v(0.87, -18.75) * mm, v(0.68, -18.71) * mm, v(0.65, -18.63) * mm, v(0.62, -18.58) * mm, v(0.59, -18.5) * mm, v(0.57, -18.32) * mm, v(0.58, -18.14) * mm, v(0.62, -18.04) * mm, v(0.61, -17.96) * mm, v(0.61, -17.87) * mm, v(0.68, -17.78) * mm, v(0.77, -17.81) * mm, v(0.85, -17.76) * mm, v(0.82, -17.53) * mm, v(0.84, -17.33) * mm, v(0.74, -17.15) * mm, v(0.68, -17.06) * mm, v(0.65, -16.97) * mm, v(0.53, -16.77) * mm, v(0.44, -16.71) * mm, v(0.34, -16.52) * mm, v(0.27, -16.46) * mm, v(0.11, -16.32) * mm, v(0, -16.4) * mm, v(-0.14, -16.42) * mm, v(-0.26, -16.65) * mm, v(-0.37, -16.62) * mm, v(-0.61, -16.63) * mm, v(-0.62, -16.63) * mm, v(-0.63, -16.63) * mm]});
            skLineSegment(sketch, "E169", {"start": v(2.37, -13.94) * mm, "end": v(2.12, -14.4) * mm});
            skPoint(sketch, "E170.orphan", {"position": v(2.15, -12.9) * mm});
            skPoint(sketch, "E171.orphan", {"position": v(-0.62, -16.63) * mm});
            skSolve(sketch);
        }
        {
            var Q0;
            Q0 = qSketchRegion(id + "F6", true);
            var Q1;
            Q1=makeQuery(id+"F5.boolean.opBoolean","SPLIT",FACE,{"disambiguationData":[TD([makeQuery(id+"F5.opExtrude","SWEPT_FACE",FACE,{"disambiguationData":[OSD([sQuery(id+"F3.wireOp",EDGE,"E141.0")])]})])],"derivedFrom":makeQuery(id+"F2.opExtrude","CAP_FACE",FACE,{"disambiguationData":[OSD([sQuery(id+"F1.wireOp",EDGE,"E138.0")])],"isStart":false})});
            extrude(context, id + "F7", {"entities" : qUnion([Q0]), "operationType" : NewBodyOperationType.REMOVE, "endBound" : BoundingType.UP_TO_SURFACE, "oppositeDirection" : true, "endBoundEntityFace" : qUnion([Q1]), "depth" : 25 * mm});
        }
        {
            var Q0;
            Q0=qCreatedBy(makeId("Top.planeOp"),FACE);
            var sketch = newSketch(context, id + "F8", { "sketchPlane" : qUnion([Q0])});
            skLineSegment(sketch, "E172.bottom", {"start": v(30, -37.5) * mm, "end": v(-30, -37.5) * mm});
            skLineSegment(sketch, "E172.top", {"start": v(30, -22.5) * mm, "end": v(6.48, -22.5) * mm});
            skLineSegment(sketch, "E172.left", {"start": v(30, -37.5) * mm, "end": v(30, -22.5) * mm});
            skLineSegment(sketch, "E172.right", {"start": v(-30, -37.5) * mm, "end": v(-30, -22.5) * mm});
            skPoint(sketch, "E172.middle", {"position": v(0, -30) * mm});
            skEllipticalArc(sketch, "E173.0", {});
            skLineSegment(sketch, "E174.trimOffspring", {"start": v(-6.48, -22.5) * mm, "end": v(-30, -22.5) * mm});
            const initialGuessF8  = {"E173.0": [0, 0, 0, 1, 0.02528772606326864, 0.014197551645338535, 2.667614786270828, 3.615570520908758]};
            skSetInitialGuess(sketch, initialGuessF8);
            skSolve(sketch);
        }
        {
            var Q0;
            Q0 = qSketchRegion(id + "F8", true);
            var Q1;
            Q1=makeQuery(id+"F5.boolean.opBoolean","SPLIT",FACE,{"disambiguationData":[TD([makeQuery(id+"F4.opExtrude","SWEPT_FACE",FACE,{"disambiguationData":[OSD([sQuery(id+"F3.wireOp",EDGE,"E139.29")])]})])],"derivedFrom":makeQuery(id+"F2.opExtrude","CAP_FACE",FACE,{"disambiguationData":[OSD([sQuery(id+"F1.wireOp",EDGE,"E138.0")])],"isStart":false})});
            extrude(context, id + "F9", {"entities" : qUnion([Q0]), "operationType" : NewBodyOperationType.ADD, "endBound" : BoundingType.UP_TO_SURFACE, "endBoundEntityFace" : qUnion([Q1]), "depth" : 25 * mm});
        }
        {
            var Q0;
            Q0=makeQuery(id+"F9.opExtrude","CAP_FACE",FACE,{"disambiguationData":[OSD([sQuery(id+"F8.wireOp",EDGE,"E172.bottom"),sQuery(id+"F8.wireOp",EDGE,"E172.top"),sQuery(id+"F8.wireOp",EDGE,"E172.left"),sQuery(id+"F8.wireOp",EDGE,"E172.right"),sQuery(id+"F8.wireOp",EDGE,"E173.0"),sQuery(id+"F8.wireOp",EDGE,"E174.trimOffspring")])],"isStart":false});
            var sketch = newSketch(context, id + "F10", { "sketchPlane" : qUnion([Q0])});
            skText(sketch, "E175", { "text": "Allenatore Ysabah92", "fontName": "Tinos-BoldItalic.ttf"});
            const initialGuessF10  = {"E175": [-0.02707, -0.03223, 1, 0, 0.00446]};
            skSetInitialGuess(sketch, initialGuessF10);
            skSolve(sketch);
        }
        {
            var Q0;
            Q0 = qSketchRegion(id + "F10", true);
            extrude(context, id + "F11", {"entities" : qUnion([Q0]), "operationType" : NewBodyOperationType.ADD, "depth" : 0.5 * mm});
        }
        {
            var Q0;
            Q0=makeQuery(id+"F9.opExtrude","SWEPT_EDGE",EDGE,{"disambiguationData":[OSD([sQuery(id+"F8.wireOp",EDGE,"E172.bottom"),sQuery(id+"F8.wireOp",EDGE,"E172.left")])]});
            var Q1;
            Q1=makeQuery(id+"F9.opExtrude","SWEPT_EDGE",EDGE,{"disambiguationData":[OSD([sQuery(id+"F8.wireOp",EDGE,"E172.top"),sQuery(id+"F8.wireOp",EDGE,"E172.left")])]});
            var Q2;
            Q2=makeQuery(id+"F9.opExtrude","SWEPT_EDGE",EDGE,{"disambiguationData":[OSD([sQuery(id+"F8.wireOp",EDGE,"E172.bottom"),sQuery(id+"F8.wireOp",EDGE,"E172.right")])]});
            var Q3;
            Q3=makeQuery(id+"F9.opExtrude","SWEPT_EDGE",EDGE,{"disambiguationData":[OSD([sQuery(id+"F8.wireOp",EDGE,"E172.right"),sQuery(id+"F8.wireOp",EDGE,"E174.trimOffspring")])]});
            var Q4;
            {var subQ0=sQuery(id+"F8.wireOp",EDGE,"E174.trimOffspring");Q4=makeQuery(id+"F9.boolean.opBoolean","SPLIT",EDGE,{"disambiguationData":[topologyDisambiguationEdgeConnected([makeQuery(id+"F2.opExtrude","SWEPT_FACE",FACE,{"disambiguationData":[OSD([sQuery(id+"F1.wireOp",EDGE,"E138.0")])]})])],"derivedFrom":makeQuery(id+"F9.opExtrude","SWEPT_EDGE",EDGE,{"disambiguationData":[OSD([sQuery(id+"F8.wireOp",EDGE,"E173.0"),subQ0])]})});}
            var Q5;
            {var subQ0=sQuery(id+"F8.wireOp",EDGE,"E172.top");Q5=makeQuery(id+"F9.boolean.opBoolean","SPLIT",EDGE,{"disambiguationData":[topologyDisambiguationEdgeConnected([makeQuery(id+"F2.opExtrude","SWEPT_FACE",FACE,{"disambiguationData":[OSD([sQuery(id+"F1.wireOp",EDGE,"E138.0")])]})])],"derivedFrom":makeQuery(id+"F9.opExtrude","SWEPT_EDGE",EDGE,{"disambiguationData":[OSD([subQ0,sQuery(id+"F8.wireOp",EDGE,"E173.0")])]})});}
            fillet(context, id + "F12", {"entities" : qUnion([Q0, Q1, Q2, Q3, Q4, Q5]), "radius" : 5 * mm, "tangentPropagation" : true, "allowEdgeOverflow" : false});
        }
        {
            var Q0;
            Q0=makeQuery(id+"F11.opExtrude","CAP_FACE",FACE,{"disambiguationData":[OSD([sQuery(id+"F10.wireOp",EDGE,"E175.sketch_text.stroke-180"),sQuery(id+"F10.wireOp",EDGE,"E175.sketch_text.stroke-181"),sQuery(id+"F10.wireOp",EDGE,"E175.sketch_text.stroke-182"),sQuery(id+"F10.wireOp",EDGE,"E175.sketch_text.stroke-183"),sQuery(id+"F10.wireOp",EDGE,"E175.sketch_text.stroke-184"),sQuery(id+"F10.wireOp",EDGE,"E175.sketch_text.stroke-185"),sQuery(id+"F10.wireOp",EDGE,"E175.sketch_text.stroke-186"),sQuery(id+"F10.wireOp",EDGE,"E175.sketch_text.stroke-187"),sQuery(id+"F10.wireOp",EDGE,"E175.sketch_text.stroke-188"),sQuery(id+"F10.wireOp",EDGE,"E175.sketch_text.stroke-189"),sQuery(id+"F10.wireOp",EDGE,"E175.sketch_text.stroke-190"),sQuery(id+"F10.wireOp",EDGE,"E175.sketch_text.stroke-191"),sQuery(id+"F10.wireOp",EDGE,"E175.sketch_text.stroke-192"),sQuery(id+"F10.wireOp",EDGE,"E175.sketch_text.stroke-193"),sQuery(id+"F10.wireOp",EDGE,"E175.sketch_text.stroke-194"),sQuery(id+"F10.wireOp",EDGE,"E175.sketch_text.stroke-195"),sQuery(id+"F10.wireOp",EDGE,"E175.sketch_text.stroke-196"),sQuery(id+"F10.wireOp",EDGE,"E175.sketch_text.stroke-197"),sQuery(id+"F10.wireOp",EDGE,"E175.sketch_text.stroke-198"),sQuery(id+"F10.wireOp",EDGE,"E175.sketch_text.stroke-199"),sQuery(id+"F10.wireOp",EDGE,"E175.sketch_text.stroke-200")])],"isStart":false});
            var Q1;
            Q1=makeQuery(id+"F11.opExtrude","CAP_FACE",FACE,{"disambiguationData":[OSD([sQuery(id+"F10.wireOp",EDGE,"E175.sketch_text.stroke-201"),sQuery(id+"F10.wireOp",EDGE,"E175.sketch_text.stroke-202"),sQuery(id+"F10.wireOp",EDGE,"E175.sketch_text.stroke-203"),sQuery(id+"F10.wireOp",EDGE,"E175.sketch_text.stroke-204"),sQuery(id+"F10.wireOp",EDGE,"E175.sketch_text.stroke-205"),sQuery(id+"F10.wireOp",EDGE,"E175.sketch_text.stroke-206"),sQuery(id+"F10.wireOp",EDGE,"E175.sketch_text.stroke-207"),sQuery(id+"F10.wireOp",EDGE,"E175.sketch_text.stroke-208"),sQuery(id+"F10.wireOp",EDGE,"E175.sketch_text.stroke-209"),sQuery(id+"F10.wireOp",EDGE,"E175.sketch_text.stroke-210"),sQuery(id+"F10.wireOp",EDGE,"E175.sketch_text.stroke-211"),sQuery(id+"F10.wireOp",EDGE,"E175.sketch_text.stroke-212"),sQuery(id+"F10.wireOp",EDGE,"E175.sketch_text.stroke-213"),sQuery(id+"F10.wireOp",EDGE,"E175.sketch_text.stroke-214"),sQuery(id+"F10.wireOp",EDGE,"E175.sketch_text.stroke-215"),sQuery(id+"F10.wireOp",EDGE,"E175.sketch_text.stroke-216"),sQuery(id+"F10.wireOp",EDGE,"E175.sketch_text.stroke-217"),sQuery(id+"F10.wireOp",EDGE,"E175.sketch_text.stroke-218"),sQuery(id+"F10.wireOp",EDGE,"E175.sketch_text.stroke-219"),sQuery(id+"F10.wireOp",EDGE,"E175.sketch_text.stroke-220"),sQuery(id+"F10.wireOp",EDGE,"E175.sketch_text.stroke-221"),sQuery(id+"F10.wireOp",EDGE,"E175.sketch_text.stroke-222"),sQuery(id+"F10.wireOp",EDGE,"E175.sketch_text.stroke-223"),sQuery(id+"F10.wireOp",EDGE,"E175.sketch_text.stroke-224"),sQuery(id+"F10.wireOp",EDGE,"E175.sketch_text.stroke-225"),sQuery(id+"F10.wireOp",EDGE,"E175.sketch_text.stroke-226"),sQuery(id+"F10.wireOp",EDGE,"E175.sketch_text.stroke-227"),sQuery(id+"F10.wireOp",EDGE,"E175.sketch_text.stroke-228"),sQuery(id+"F10.wireOp",EDGE,"E175.sketch_text.stroke-229")])],"isStart":false});
            var Q2;
            Q2=makeQuery(id+"F11.opExtrude","CAP_FACE",FACE,{"disambiguationData":[OSD([sQuery(id+"F10.wireOp",EDGE,"E175.sketch_text.stroke-230"),sQuery(id+"F10.wireOp",EDGE,"E175.sketch_text.stroke-231"),sQuery(id+"F10.wireOp",EDGE,"E175.sketch_text.stroke-232"),sQuery(id+"F10.wireOp",EDGE,"E175.sketch_text.stroke-233"),sQuery(id+"F10.wireOp",EDGE,"E175.sketch_text.stroke-234"),sQuery(id+"F10.wireOp",EDGE,"E175.sketch_text.stroke-235"),sQuery(id+"F10.wireOp",EDGE,"E175.sketch_text.stroke-236"),sQuery(id+"F10.wireOp",EDGE,"E175.sketch_text.stroke-237"),sQuery(id+"F10.wireOp",EDGE,"E175.sketch_text.stroke-238"),sQuery(id+"F10.wireOp",EDGE,"E175.sketch_text.stroke-239"),sQuery(id+"F10.wireOp",EDGE,"E175.sketch_text.stroke-240"),sQuery(id+"F10.wireOp",EDGE,"E175.sketch_text.stroke-241"),sQuery(id+"F10.wireOp",EDGE,"E175.sketch_text.stroke-242"),sQuery(id+"F10.wireOp",EDGE,"E175.sketch_text.stroke-243"),sQuery(id+"F10.wireOp",EDGE,"E175.sketch_text.stroke-244"),sQuery(id+"F10.wireOp",EDGE,"E175.sketch_text.stroke-245"),sQuery(id+"F10.wireOp",EDGE,"E175.sketch_text.stroke-246"),sQuery(id+"F10.wireOp",EDGE,"E175.sketch_text.stroke-247"),sQuery(id+"F10.wireOp",EDGE,"E175.sketch_text.stroke-248"),sQuery(id+"F10.wireOp",EDGE,"E175.sketch_text.stroke-249"),sQuery(id+"F10.wireOp",EDGE,"E175.sketch_text.stroke-250"),sQuery(id+"F10.wireOp",EDGE,"E175.sketch_text.stroke-251"),sQuery(id+"F10.wireOp",EDGE,"E175.sketch_text.stroke-252"),sQuery(id+"F10.wireOp",EDGE,"E175.sketch_text.stroke-253")])],"isStart":false});
            var Q3;
            Q3=makeQuery(id+"F11.opExtrude","CAP_FACE",FACE,{"disambiguationData":[OSD([sQuery(id+"F10.wireOp",EDGE,"E175.sketch_text.stroke-254"),sQuery(id+"F10.wireOp",EDGE,"E175.sketch_text.stroke-255"),sQuery(id+"F10.wireOp",EDGE,"E175.sketch_text.stroke-256"),sQuery(id+"F10.wireOp",EDGE,"E175.sketch_text.stroke-257"),sQuery(id+"F10.wireOp",EDGE,"E175.sketch_text.stroke-258"),sQuery(id+"F10.wireOp",EDGE,"E175.sketch_text.stroke-259"),sQuery(id+"F10.wireOp",EDGE,"E175.sketch_text.stroke-260"),sQuery(id+"F10.wireOp",EDGE,"E175.sketch_text.stroke-261"),sQuery(id+"F10.wireOp",EDGE,"E175.sketch_text.stroke-262"),sQuery(id+"F10.wireOp",EDGE,"E175.sketch_text.stroke-263"),sQuery(id+"F10.wireOp",EDGE,"E175.sketch_text.stroke-264"),sQuery(id+"F10.wireOp",EDGE,"E175.sketch_text.stroke-265"),sQuery(id+"F10.wireOp",EDGE,"E175.sketch_text.stroke-266"),sQuery(id+"F10.wireOp",EDGE,"E175.sketch_text.stroke-267"),sQuery(id+"F10.wireOp",EDGE,"E175.sketch_text.stroke-268"),sQuery(id+"F10.wireOp",EDGE,"E175.sketch_text.stroke-269"),sQuery(id+"F10.wireOp",EDGE,"E175.sketch_text.stroke-270"),sQuery(id+"F10.wireOp",EDGE,"E175.sketch_text.stroke-271"),sQuery(id+"F10.wireOp",EDGE,"E175.sketch_text.stroke-272"),sQuery(id+"F10.wireOp",EDGE,"E175.sketch_text.stroke-273"),sQuery(id+"F10.wireOp",EDGE,"E175.sketch_text.stroke-274"),sQuery(id+"F10.wireOp",EDGE,"E175.sketch_text.stroke-275"),sQuery(id+"F10.wireOp",EDGE,"E175.sketch_text.stroke-276"),sQuery(id+"F10.wireOp",EDGE,"E175.sketch_text.stroke-277"),sQuery(id+"F10.wireOp",EDGE,"E175.sketch_text.stroke-278")])],"isStart":false});
            var Q4;
            Q4=makeQuery(id+"F11.opExtrude","CAP_FACE",FACE,{"disambiguationData":[OSD([sQuery(id+"F10.wireOp",EDGE,"E175.sketch_text.stroke-279"),sQuery(id+"F10.wireOp",EDGE,"E175.sketch_text.stroke-280"),sQuery(id+"F10.wireOp",EDGE,"E175.sketch_text.stroke-281"),sQuery(id+"F10.wireOp",EDGE,"E175.sketch_text.stroke-282"),sQuery(id+"F10.wireOp",EDGE,"E175.sketch_text.stroke-283"),sQuery(id+"F10.wireOp",EDGE,"E175.sketch_text.stroke-284"),sQuery(id+"F10.wireOp",EDGE,"E175.sketch_text.stroke-285"),sQuery(id+"F10.wireOp",EDGE,"E175.sketch_text.stroke-286"),sQuery(id+"F10.wireOp",EDGE,"E175.sketch_text.stroke-287"),sQuery(id+"F10.wireOp",EDGE,"E175.sketch_text.stroke-288"),sQuery(id+"F10.wireOp",EDGE,"E175.sketch_text.stroke-289"),sQuery(id+"F10.wireOp",EDGE,"E175.sketch_text.stroke-290"),sQuery(id+"F10.wireOp",EDGE,"E175.sketch_text.stroke-291"),sQuery(id+"F10.wireOp",EDGE,"E175.sketch_text.stroke-292"),sQuery(id+"F10.wireOp",EDGE,"E175.sketch_text.stroke-293"),sQuery(id+"F10.wireOp",EDGE,"E175.sketch_text.stroke-294"),sQuery(id+"F10.wireOp",EDGE,"E175.sketch_text.stroke-295"),sQuery(id+"F10.wireOp",EDGE,"E175.sketch_text.stroke-296"),sQuery(id+"F10.wireOp",EDGE,"E175.sketch_text.stroke-297"),sQuery(id+"F10.wireOp",EDGE,"E175.sketch_text.stroke-298"),sQuery(id+"F10.wireOp",EDGE,"E175.sketch_text.stroke-299"),sQuery(id+"F10.wireOp",EDGE,"E175.sketch_text.stroke-300"),sQuery(id+"F10.wireOp",EDGE,"E175.sketch_text.stroke-301"),sQuery(id+"F10.wireOp",EDGE,"E175.sketch_text.stroke-302")])],"isStart":false});
            var Q5;
            Q5=makeQuery(id+"F11.opExtrude","CAP_FACE",FACE,{"disambiguationData":[OSD([sQuery(id+"F10.wireOp",EDGE,"E175.sketch_text.stroke-303"),sQuery(id+"F10.wireOp",EDGE,"E175.sketch_text.stroke-304"),sQuery(id+"F10.wireOp",EDGE,"E175.sketch_text.stroke-305"),sQuery(id+"F10.wireOp",EDGE,"E175.sketch_text.stroke-306"),sQuery(id+"F10.wireOp",EDGE,"E175.sketch_text.stroke-307"),sQuery(id+"F10.wireOp",EDGE,"E175.sketch_text.stroke-308"),sQuery(id+"F10.wireOp",EDGE,"E175.sketch_text.stroke-309"),sQuery(id+"F10.wireOp",EDGE,"E175.sketch_text.stroke-310"),sQuery(id+"F10.wireOp",EDGE,"E175.sketch_text.stroke-311"),sQuery(id+"F10.wireOp",EDGE,"E175.sketch_text.stroke-312"),sQuery(id+"F10.wireOp",EDGE,"E175.sketch_text.stroke-313"),sQuery(id+"F10.wireOp",EDGE,"E175.sketch_text.stroke-314"),sQuery(id+"F10.wireOp",EDGE,"E175.sketch_text.stroke-315"),sQuery(id+"F10.wireOp",EDGE,"E175.sketch_text.stroke-316"),sQuery(id+"F10.wireOp",EDGE,"E175.sketch_text.stroke-317"),sQuery(id+"F10.wireOp",EDGE,"E175.sketch_text.stroke-318"),sQuery(id+"F10.wireOp",EDGE,"E175.sketch_text.stroke-319"),sQuery(id+"F10.wireOp",EDGE,"E175.sketch_text.stroke-320"),sQuery(id+"F10.wireOp",EDGE,"E175.sketch_text.stroke-321"),sQuery(id+"F10.wireOp",EDGE,"E175.sketch_text.stroke-322"),sQuery(id+"F10.wireOp",EDGE,"E175.sketch_text.stroke-323"),sQuery(id+"F10.wireOp",EDGE,"E175.sketch_text.stroke-324")])],"isStart":false});
            var Q6;
            Q6=makeQuery(id+"F11.opExtrude","CAP_FACE",FACE,{"disambiguationData":[OSD([sQuery(id+"F10.wireOp",EDGE,"E175.sketch_text.stroke-325"),sQuery(id+"F10.wireOp",EDGE,"E175.sketch_text.stroke-326"),sQuery(id+"F10.wireOp",EDGE,"E175.sketch_text.stroke-327"),sQuery(id+"F10.wireOp",EDGE,"E175.sketch_text.stroke-328"),sQuery(id+"F10.wireOp",EDGE,"E175.sketch_text.stroke-329"),sQuery(id+"F10.wireOp",EDGE,"E175.sketch_text.stroke-330"),sQuery(id+"F10.wireOp",EDGE,"E175.sketch_text.stroke-331"),sQuery(id+"F10.wireOp",EDGE,"E175.sketch_text.stroke-332"),sQuery(id+"F10.wireOp",EDGE,"E175.sketch_text.stroke-333"),sQuery(id+"F10.wireOp",EDGE,"E175.sketch_text.stroke-334"),sQuery(id+"F10.wireOp",EDGE,"E175.sketch_text.stroke-335"),sQuery(id+"F10.wireOp",EDGE,"E175.sketch_text.stroke-336"),sQuery(id+"F10.wireOp",EDGE,"E175.sketch_text.stroke-337"),sQuery(id+"F10.wireOp",EDGE,"E175.sketch_text.stroke-338"),sQuery(id+"F10.wireOp",EDGE,"E175.sketch_text.stroke-339"),sQuery(id+"F10.wireOp",EDGE,"E175.sketch_text.stroke-340"),sQuery(id+"F10.wireOp",EDGE,"E175.sketch_text.stroke-341"),sQuery(id+"F10.wireOp",EDGE,"E175.sketch_text.stroke-342"),sQuery(id+"F10.wireOp",EDGE,"E175.sketch_text.stroke-343"),sQuery(id+"F10.wireOp",EDGE,"E175.sketch_text.stroke-344"),sQuery(id+"F10.wireOp",EDGE,"E175.sketch_text.stroke-345"),sQuery(id+"F10.wireOp",EDGE,"E175.sketch_text.stroke-346"),sQuery(id+"F10.wireOp",EDGE,"E175.sketch_text.stroke-347"),sQuery(id+"F10.wireOp",EDGE,"E175.sketch_text.stroke-348"),sQuery(id+"F10.wireOp",EDGE,"E175.sketch_text.stroke-349"),sQuery(id+"F10.wireOp",EDGE,"E175.sketch_text.stroke-350")])],"isStart":false});
            var Q7;
            Q7=makeQuery(id+"F11.opExtrude","CAP_FACE",FACE,{"disambiguationData":[OSD([sQuery(id+"F10.wireOp",EDGE,"E175.sketch_text.stroke-351"),sQuery(id+"F10.wireOp",EDGE,"E175.sketch_text.stroke-352"),sQuery(id+"F10.wireOp",EDGE,"E175.sketch_text.stroke-353"),sQuery(id+"F10.wireOp",EDGE,"E175.sketch_text.stroke-354"),sQuery(id+"F10.wireOp",EDGE,"E175.sketch_text.stroke-355"),sQuery(id+"F10.wireOp",EDGE,"E175.sketch_text.stroke-356"),sQuery(id+"F10.wireOp",EDGE,"E175.sketch_text.stroke-357"),sQuery(id+"F10.wireOp",EDGE,"E175.sketch_text.stroke-358"),sQuery(id+"F10.wireOp",EDGE,"E175.sketch_text.stroke-359"),sQuery(id+"F10.wireOp",EDGE,"E175.sketch_text.stroke-360"),sQuery(id+"F10.wireOp",EDGE,"E175.sketch_text.stroke-361"),sQuery(id+"F10.wireOp",EDGE,"E175.sketch_text.stroke-362"),sQuery(id+"F10.wireOp",EDGE,"E175.sketch_text.stroke-363"),sQuery(id+"F10.wireOp",EDGE,"E175.sketch_text.stroke-364"),sQuery(id+"F10.wireOp",EDGE,"E175.sketch_text.stroke-365"),sQuery(id+"F10.wireOp",EDGE,"E175.sketch_text.stroke-366"),sQuery(id+"F10.wireOp",EDGE,"E175.sketch_text.stroke-367"),sQuery(id+"F10.wireOp",EDGE,"E175.sketch_text.stroke-368"),sQuery(id+"F10.wireOp",EDGE,"E175.sketch_text.stroke-369"),sQuery(id+"F10.wireOp",EDGE,"E175.sketch_text.stroke-370")])],"isStart":false});
            var Q8;
            Q8=makeQuery(id+"F5.opExtrude","CAP_FACE",FACE,{"disambiguationData":[OSD([sQuery(id+"F3.wireOp",EDGE,"E139.45"),sQuery(id+"F3.wireOp",EDGE,"E139.47"),sQuery(id+"F3.wireOp",EDGE,"E139.48"),sQuery(id+"F3.wireOp",EDGE,"E139.55")])],"isStart":false});
            extrude(context, id + "F13", {"entities" : qUnion([Q0, Q1, Q2, Q3, Q4, Q5, Q6, Q7, Q8]), "operationType" : NewBodyOperationType.ADD, "depth" : 0.5 * mm});
        }
        {
            var Q0;
            Q0=makeQuery(id+"F2.opExtrude","SWEPT_BODY",BODY,{"disambiguationData":[OSD([sQuery(id+"F1.wireOp",EDGE,"E138.0")])]});
            var Q1;
            Q1=qCreatedBy(makeId("Origin.pointOp"),VERTEX);
            transform(context, id + "F14", {"entities" : qUnion([Q0]), "transformType" : TransformType.SCALE_UNIFORMLY, "scale" : 2.5, "scalePoint" : qUnion([Q1]), "makeCopy" : false});
        }
        {
            var Q0;
            Q0=qCreatedBy(makeId("Right.planeOp"),FACE);
            var sketch = newSketch(context, id + "F15", { "sketchPlane" : qUnion([Q0])});
            skLineSegment(sketch, "E176.bottom", {"start": v(82.49, 5.5) * mm, "end": v(-140.5, 5.5) * mm});
            skLineSegment(sketch, "E176.top", {"start": v(82.49, 29.47) * mm, "end": v(-140.5, 29.47) * mm});
            skLineSegment(sketch, "E176.left", {"start": v(82.49, 5.5) * mm, "end": v(82.49, 29.47) * mm});
            skLineSegment(sketch, "E176.right", {"start": v(-140.5, 5.5) * mm, "end": v(-140.5, 29.47) * mm});
            skSolve(sketch);
        }
        {
            var Q0;
            Q0 = qSketchRegion(id + "F15", true);
            extrude(context, id + "F16", {"entities" : qUnion([Q0]), "operationType" : NewBodyOperationType.REMOVE, "endBound" : BoundingType.THROUGH_ALL, "oppositeDirection" : true, "depth" : 25 * mm, "hasSecondDirection" : true, "secondDirectionBound" : SecondDirectionBoundingType.THROUGH_ALL, "secondDirectionOppositeDirection" : false, "secondDirectionDepth" : 25 * mm});
        }
        {
            var Q0;
            {var subQ1=sQuery(id+"F10.wireOp",EDGE,"E175.sketch_text.stroke-180");Q0=makeQuery(id+"F16.boolean.opBoolean","COPY",FACE,{"disambiguationData":[TD([makeQuery(id+"F11.opExtrude","SWEPT_FACE",FACE,{"disambiguationData":[OSD([subQ1])]})])],"derivedFrom":makeQuery(id+"F16.opExtrude","SWEPT_FACE",FACE,{"disambiguationData":[OSD([sQuery(id+"F15.wireOp",EDGE,"E176.bottom")])]})});}
            var Q1;
            {var subQ24=sQuery(id+"F10.wireOp",EDGE,"E175.sketch_text.stroke-201");Q1=makeQuery(id+"F16.boolean.opBoolean","COPY",FACE,{"disambiguationData":[TD([makeQuery(id+"F11.opExtrude","SWEPT_FACE",FACE,{"disambiguationData":[OSD([subQ24])]})])],"derivedFrom":makeQuery(id+"F16.opExtrude","SWEPT_FACE",FACE,{"disambiguationData":[OSD([sQuery(id+"F15.wireOp",EDGE,"E176.bottom")])]})});}
            var Q2;
            {var subQ20=sQuery(id+"F10.wireOp",EDGE,"E175.sketch_text.stroke-230");Q2=makeQuery(id+"F16.boolean.opBoolean","COPY",FACE,{"disambiguationData":[TD([makeQuery(id+"F11.opExtrude","SWEPT_FACE",FACE,{"disambiguationData":[OSD([subQ20])]})])],"derivedFrom":makeQuery(id+"F16.opExtrude","SWEPT_FACE",FACE,{"disambiguationData":[OSD([sQuery(id+"F15.wireOp",EDGE,"E176.bottom")])]})});}
            var Q3;
            {var subQ21=sQuery(id+"F10.wireOp",EDGE,"E175.sketch_text.stroke-254");Q3=makeQuery(id+"F16.boolean.opBoolean","COPY",FACE,{"disambiguationData":[TD([makeQuery(id+"F11.opExtrude","SWEPT_FACE",FACE,{"disambiguationData":[OSD([subQ21])]})])],"derivedFrom":makeQuery(id+"F16.opExtrude","SWEPT_FACE",FACE,{"disambiguationData":[OSD([sQuery(id+"F15.wireOp",EDGE,"E176.bottom")])]})});}
            var Q4;
            {var subQ15=sQuery(id+"F10.wireOp",EDGE,"E175.sketch_text.stroke-279");Q4=makeQuery(id+"F16.boolean.opBoolean","COPY",FACE,{"disambiguationData":[TD([makeQuery(id+"F11.opExtrude","SWEPT_FACE",FACE,{"disambiguationData":[OSD([subQ15])]})])],"derivedFrom":makeQuery(id+"F16.opExtrude","SWEPT_FACE",FACE,{"disambiguationData":[OSD([sQuery(id+"F15.wireOp",EDGE,"E176.bottom")])]})});}
            var Q5;
            {var subQ20=sQuery(id+"F10.wireOp",EDGE,"E175.sketch_text.stroke-303");Q5=makeQuery(id+"F16.boolean.opBoolean","COPY",FACE,{"disambiguationData":[TD([makeQuery(id+"F11.opExtrude","SWEPT_FACE",FACE,{"disambiguationData":[OSD([subQ20])]})])],"derivedFrom":makeQuery(id+"F16.opExtrude","SWEPT_FACE",FACE,{"disambiguationData":[OSD([sQuery(id+"F15.wireOp",EDGE,"E176.bottom")])]})});}
            var Q6;
            {var subQ12=sQuery(id+"F10.wireOp",EDGE,"E175.sketch_text.stroke-325");Q6=makeQuery(id+"F16.boolean.opBoolean","COPY",FACE,{"disambiguationData":[TD([makeQuery(id+"F11.opExtrude","SWEPT_FACE",FACE,{"disambiguationData":[OSD([subQ12])]})])],"derivedFrom":makeQuery(id+"F16.opExtrude","SWEPT_FACE",FACE,{"disambiguationData":[OSD([sQuery(id+"F15.wireOp",EDGE,"E176.bottom")])]})});}
            var Q7;
            {var subQ18=sQuery(id+"F10.wireOp",EDGE,"E175.sketch_text.stroke-351");Q7=makeQuery(id+"F16.boolean.opBoolean","COPY",FACE,{"disambiguationData":[TD([makeQuery(id+"F11.opExtrude","SWEPT_FACE",FACE,{"disambiguationData":[OSD([subQ18])]})])],"derivedFrom":makeQuery(id+"F16.opExtrude","SWEPT_FACE",FACE,{"disambiguationData":[OSD([sQuery(id+"F15.wireOp",EDGE,"E176.bottom")])]})});}
            var Q8;
            {var subQ3=sQuery(id+"F3.wireOp",EDGE,"E139.45");Q8=makeQuery(id+"F16.boolean.opBoolean","COPY",FACE,{"disambiguationData":[TD([makeQuery(id+"F5.opExtrude","SWEPT_FACE",FACE,{"disambiguationData":[OSD([subQ3])]})])],"derivedFrom":makeQuery(id+"F16.opExtrude","SWEPT_FACE",FACE,{"disambiguationData":[OSD([sQuery(id+"F15.wireOp",EDGE,"E176.bottom")])]})});}
            extrude(context, id + "F17", {"entities" : qUnion([Q0, Q1, Q2, Q3, Q4, Q5, Q6, Q7, Q8]), "operationType" : NewBodyOperationType.ADD, "depth" : 0.5 * mm});
        }
        {
            var Q0;
            Q0=makeQuery(id+"F9.boolean.opBoolean","MERGE",FACE,{"derivedFrom":[makeQuery(id+"F2.opExtrude","CAP_FACE",FACE,{"disambiguationData":[OSD([sQuery(id+"F1.wireOp",EDGE,"E138.0")])],"isStart":true}),makeQuery(id+"F9.opExtrude","CAP_FACE",FACE,{"disambiguationData":[OSD([sQuery(id+"F8.wireOp",EDGE,"E172.bottom"),sQuery(id+"F8.wireOp",EDGE,"E172.top"),sQuery(id+"F8.wireOp",EDGE,"E172.left"),sQuery(id+"F8.wireOp",EDGE,"E172.right"),sQuery(id+"F8.wireOp",EDGE,"E173.0"),sQuery(id+"F8.wireOp",EDGE,"E174.trimOffspring")])],"isStart":true})]});
            extrude(context, id + "F18", {"entities" : qUnion([Q0]), "operationType" : NewBodyOperationType.ADD, "depth" : 1 * mm});
        }
        {
            var Q0;
            {var subQ0=sQuery(id+"F8.wireOp",EDGE,"E174.trimOffspring");var subQ1=sQuery(id+"F8.wireOp",EDGE,"E172.right");var subQ2=sQuery(id+"F8.wireOp",EDGE,"E172.left");var subQ3=sQuery(id+"F8.wireOp",EDGE,"E172.bottom");var subQ4=sQuery(id+"F8.wireOp",EDGE,"E172.top");Q0=makeQuery(id+"F11.boolean.opBoolean","SPLIT",FACE,{"disambiguationData":[TD([makeQuery(id+"F2.opExtrude","SWEPT_FACE",FACE,{"disambiguationData":[OSD([sQuery(id+"F1.wireOp",EDGE,"E138.0")])]})])],"derivedFrom":makeQuery(id+"F9.opExtrude","CAP_FACE",FACE,{"disambiguationData":[OSD([subQ3,subQ4,subQ2,subQ1,sQuery(id+"F8.wireOp",EDGE,"E173.0"),subQ0])],"isStart":false})});}
            var sketch = newSketch(context, id + "F19", { "sketchPlane" : qUnion([Q0])});
            skCircle(sketch, "E177.cCircle", {"center": v(37.5, -81.75) * mm, "radius": 2.85 * mm, "construction": true});
            skLineSegment(sketch, "E177.0", {"start": v(35.85, -78.9) * mm, "end": v(39.15, -78.9) * mm});
            skLineSegment(sketch, "E177.1", {"start": v(39.15, -78.9) * mm, "end": v(40.8, -81.75) * mm});
            skLineSegment(sketch, "E177.2", {"start": v(40.8, -81.75) * mm, "end": v(39.15, -84.6) * mm});
            skLineSegment(sketch, "E177.3", {"start": v(39.15, -84.6) * mm, "end": v(35.85, -84.6) * mm});
            skLineSegment(sketch, "E177.4", {"start": v(35.85, -84.6) * mm, "end": v(34.2, -81.75) * mm});
            skLineSegment(sketch, "E177.5", {"start": v(34.2, -81.75) * mm, "end": v(35.85, -78.9) * mm});
            skPoint(sketch, "E177.0.midPoint", {"position": v(37.5, -78.9) * mm});
            skLineSegment(sketch, "E178", {"start": v(0, 63.22) * mm, "end": v(0, -93.75) * mm, "construction": true});
            skLineSegment(sketch, "E179", {"start": v(75, -75) * mm, "end": v(0, -75) * mm, "construction": true});
            skLineSegment(sketch, "E180", {"start": v(37.5, -75.7) * mm, "end": v(37.5, -93.75) * mm, "construction": true});
            skPoint(sketch, "E180.startSnap0", {"position": v(37.5, -75) * mm});
            skLineSegment(sketch, "E181.MirrorCS", {"start": v(-39.15, -78.9) * mm, "end": v(-40.8, -81.75) * mm});
            skLineSegment(sketch, "E182.MirrorCS", {"start": v(-35.85, -78.9) * mm, "end": v(-39.15, -78.9) * mm});
            skLineSegment(sketch, "E183.MirrorCS", {"start": v(-34.2, -81.75) * mm, "end": v(-35.85, -78.9) * mm});
            skLineSegment(sketch, "E184.MirrorCS", {"start": v(-35.85, -84.6) * mm, "end": v(-34.2, -81.75) * mm});
            skPoint(sketch, "E185.MirrorP", {"position": v(-37.5, -78.9) * mm});
            skCircle(sketch, "E186.MirrorC", {"center": v(-37.5, -81.75) * mm, "radius": 2.85 * mm, "construction": true});
            skLineSegment(sketch, "E187.MirrorCS", {"start": v(-39.15, -84.6) * mm, "end": v(-35.85, -84.6) * mm});
            skLineSegment(sketch, "E188.MirrorCS", {"start": v(-40.8, -81.75) * mm, "end": v(-39.15, -84.6) * mm});
            skLineSegment(sketch, "E189", {"start": v(-37.5, -81.75) * mm, "end": v(37.5, -81.75) * mm, "construction": true});
            skCircle(sketch, "E190.cCircle", {"center": v(0, -81.75) * mm, "radius": 2.85 * mm, "construction": true});
            skLineSegment(sketch, "E190.0", {"start": v(-1.65, -78.9) * mm, "end": v(1.65, -78.9) * mm});
            skLineSegment(sketch, "E190.1", {"start": v(1.65, -78.9) * mm, "end": v(3.3, -81.75) * mm});
            skLineSegment(sketch, "E190.2", {"start": v(3.3, -81.75) * mm, "end": v(1.65, -84.6) * mm});
            skLineSegment(sketch, "E190.3", {"start": v(1.65, -84.6) * mm, "end": v(-1.65, -84.6) * mm});
            skLineSegment(sketch, "E190.4", {"start": v(-1.65, -84.6) * mm, "end": v(-3.3, -81.75) * mm});
            skLineSegment(sketch, "E190.5", {"start": v(-3.3, -81.75) * mm, "end": v(-1.65, -78.9) * mm});
            skPoint(sketch, "E190.0.midPoint", {"position": v(0, -78.9) * mm});
            skSolve(sketch);
        }
        {
            var Q0;
            Q0 = qSketchRegion(id + "F19", true);
            extrude(context, id + "F20", {"entities" : qUnion([Q0]), "operationType" : NewBodyOperationType.REMOVE, "oppositeDirection" : true, "depth" : 4 * mm, "hasSecondDirection" : true, "secondDirectionOppositeDirection" : true, "secondDirectionDepth" : 1 * mm});
        }
        {
            var Q0;
            {var subQ0=sQuery(id+"F8.wireOp",EDGE,"E172.bottom");Q0=makeQuery(id+"F18.boolean.opBoolean","MERGE",FACE,{"derivedFrom":[makeQuery(id+"F9.opExtrude","SWEPT_FACE",FACE,{"disambiguationData":[OSD([subQ0])]}),makeQuery(id+"F18.opExtrude","SWEPT_FACE",FACE,{"disambiguationData":[OSD([subQ0])]})]});}
            var sketch = newSketch(context, id + "F21", { "sketchPlane" : qUnion([Q0])});
            skLineSegment(sketch, "E191.0", {"start": v(39.15, 5) * mm, "end": v(35.85, 5) * mm, "construction": true});
            skLineSegment(sketch, "E192.0", {"start": v(40.8, 5) * mm, "end": v(39.15, 5) * mm, "construction": true});
            skLineSegment(sketch, "E193.0", {"start": v(34.2, 5) * mm, "end": v(35.85, 5) * mm, "construction": true});
            skLineSegment(sketch, "E194.bottom", {"start": v(34.2, 4) * mm, "end": v(40.8, 4) * mm});
            skLineSegment(sketch, "E194.top", {"start": v(34.2, 1) * mm, "end": v(40.8, 1) * mm});
            skLineSegment(sketch, "E194.left", {"start": v(34.2, 4) * mm, "end": v(34.2, 1) * mm});
            skLineSegment(sketch, "E194.right", {"start": v(40.8, 4) * mm, "end": v(40.8, 1) * mm});
            skLineSegment(sketch, "E195.MirrorCS", {"start": v(-40.8, 4) * mm, "end": v(-40.8, 1) * mm});
            skLineSegment(sketch, "E196.MirrorCS", {"start": v(-34.2, 4) * mm, "end": v(-34.2, 1) * mm});
            skLineSegment(sketch, "E197.MirrorCS", {"start": v(-34.2, 4) * mm, "end": v(-40.8, 4) * mm});
            skLineSegment(sketch, "E198.MirrorCS", {"start": v(-34.2, 1) * mm, "end": v(-40.8, 1) * mm});
            skLineSegment(sketch, "E199", {"start": v(0, -1) * mm, "end": v(0, 6.47) * mm, "construction": true});
            skPoint(sketch, "E199.endSnap0", {"position": v(0, -1) * mm});
            skLineSegment(sketch, "E200.0", {"start": v(-3.3, 5) * mm, "end": v(-1.65, 5) * mm, "construction": true});
            skLineSegment(sketch, "E201.0", {"start": v(3.3, 5) * mm, "end": v(1.65, 5) * mm, "construction": true});
            skLineSegment(sketch, "E202.bottom", {"start": v(-3.3, 4) * mm, "end": v(3.3, 4) * mm});
            skLineSegment(sketch, "E202.top", {"start": v(-3.3, 1) * mm, "end": v(3.3, 1) * mm});
            skLineSegment(sketch, "E202.left", {"start": v(-3.3, 4) * mm, "end": v(-3.3, 1) * mm});
            skLineSegment(sketch, "E202.right", {"start": v(3.3, 4) * mm, "end": v(3.3, 1) * mm});
            skSolve(sketch);
        }
        {
            var Q0;
            Q0 = qSketchRegion(id + "F21", true);
            extrude(context, id + "F22", {"entities" : qUnion([Q0]), "operationType" : NewBodyOperationType.REMOVE, "oppositeDirection" : true, "depth" : 12 * mm});
        }
        {
            var Q0;
            Q0=makeQuery(id+"F18.opExtrude","CAP_FACE",FACE,{"disambiguationData":[OSD([sQuery(id+"F1.wireOp",EDGE,"E138.0"),sQuery(id+"F8.wireOp",EDGE,"E172.bottom"),sQuery(id+"F8.wireOp",EDGE,"E172.top"),sQuery(id+"F8.wireOp",EDGE,"E172.left"),sQuery(id+"F8.wireOp",EDGE,"E172.right"),sQuery(id+"F8.wireOp",EDGE,"E173.0"),sQuery(id+"F8.wireOp",EDGE,"E174.trimOffspring")])],"isStart":false});
            var sketch = newSketch(context, id + "F23", { "sketchPlane" : qUnion([Q0])});
            skCircle(sketch, "E203.0", {"center": v(37.5, 81.75) * mm, "radius": 2.85 * mm, "construction": true});
            skCircle(sketch, "E204.0", {"center": v(0, 81.75) * mm, "radius": 2.85 * mm, "construction": true});
            skCircle(sketch, "E205.0", {"center": v(-37.5, 81.75) * mm, "radius": 2.85 * mm, "construction": true});
            skCircle(sketch, "E206", {"center": v(-37.5, 81.75) * mm, "radius": 1.75 * mm});
            skCircle(sketch, "E207", {"center": v(0, 81.75) * mm, "radius": 1.75 * mm});
            skCircle(sketch, "E208", {"center": v(37.5, 81.75) * mm, "radius": 1.75 * mm});
            skSolve(sketch);
        }
        {
            var Q0;
            Q0 = qSketchRegion(id + "F23", true);
            extrude(context, id + "F24", {"entities" : qUnion([Q0]), "operationType" : NewBodyOperationType.REMOVE, "endBound" : BoundingType.UP_TO_NEXT, "oppositeDirection" : true, "depth" : 25 * mm});
        }
        {
            var Q0;
            Q0=qCreatedBy(makeId("Right.planeOp"),FACE);
            var sketch = newSketch(context, id + "F25", { "sketchPlane" : qUnion([Q0])});
            skLineSegment(sketch, "E209.0", {"start": v(-93.75, -1) * mm, "end": v(-93.75, 5) * mm, "construction": true});
            skLineSegment(sketch, "E210.0", {"start": v(-56.25, 5) * mm, "end": v(-56.25, -1) * mm, "construction": true});
            skLineSegment(sketch, "E211", {"start": v(-93.75, -1) * mm, "end": v(-90.6, -18.89) * mm});
            skLineSegment(sketch, "E212", {"start": v(-93.75, -1) * mm, "end": v(-93.75, -61.43) * mm, "construction": true});
            skLineSegment(sketch, "E213", {"start": v(-93.75, -1) * mm, "end": v(-58.25, -1) * mm});
            skLineSegment(sketch, "E214", {"start": v(-58.25, -1) * mm, "end": v(-58.25, -4) * mm});
            skLineSegment(sketch, "E215", {"start": v(-58.25, -4) * mm, "end": v(-63.75, -4) * mm});
            skLineSegment(sketch, "E216", {"start": v(-63.75, -14.15) * mm, "end": v(-90.6, -18.89) * mm});
            skLineSegment(sketch, "E217", {"start": v(-63.75, -4) * mm, "end": v(-63.75, -14.15) * mm});
            skSolve(sketch);
        }
        {
            var Q0;
            Q0 = qSketchRegion(id + "F25", true);
            extrude(context, id + "F26", {"entities" : qUnion([Q0]), "depth" : 50 * mm, "hasSecondDirection" : true, "secondDirectionOppositeDirection" : true, "secondDirectionDepth" : 50 * mm});
        }
        {
            var Q0;
            Q0=makeQuery(id+"F26.opExtrude","CAP_FACE",FACE,{"disambiguationData":[OSD([sQuery(id+"F25.wireOp",EDGE,"E211"),sQuery(id+"F25.wireOp",EDGE,"E213"),sQuery(id+"F25.wireOp",EDGE,"E214"),sQuery(id+"F25.wireOp",EDGE,"E215"),sQuery(id+"F25.wireOp",EDGE,"1OioyCbx-q9Q7-nHP9-YkS4-9Z9t0t7gQg5l"),sQuery(id+"F25.wireOp",EDGE,"229q1Jfy-q8wp-kKCn-ngpl-7M3xq4eLCR7K"),sQuery(id+"F25.wireOp",EDGE,"Qlslnc4M-Edoe-GGZH-Bjeu-Gqfiu7u9IlMq")])],"isStart":false});
            var sketch = newSketch(context, id + "F27", { "sketchPlane" : qUnion([Q0])});
            skLineSegment(sketch, "E218.0", {"start": v(-93.75, -1) * mm, "end": v(-90.6, -18.89) * mm});
            skLineSegment(sketch, "E219.0", {"start": v(-93.75, -1) * mm, "end": v(-93.75, 5) * mm});
            skLineSegment(sketch, "E220", {"start": v(-90.6, -18.89) * mm, "end": v(-93.55, -19.4) * mm});
            skLineSegment(sketch, "E221", {"start": v(-93.55, -19.4) * mm, "end": v(-97.73, 4.3) * mm});
            skLineSegment(sketch, "E222", {"start": v(-93.75, 5) * mm, "end": v(-97.73, 4.3) * mm});
            skSolve(sketch);
        }
        {
            var Q0;
            Q0 = qSketchRegion(id + "F27", true);
            extrude(context, id + "F28", {"entities" : qUnion([Q0]), "operationType" : NewBodyOperationType.ADD, "oppositeDirection" : true, "depth" : 100 * mm});
        }
        {
            var Q0;
            Q0=makeQuery(id+"F26.opExtrude","SWEPT_FACE",FACE,{"disambiguationData":[OSD([sQuery(id+"F25.wireOp",EDGE,"E213")])]});
            var sketch = newSketch(context, id + "F29", { "sketchPlane" : qUnion([Q0])});
            skCircle(sketch, "E223.0", {"center": v(0, -81.75) * mm, "radius": 1.75 * mm});
            skCircle(sketch, "E224.0", {"center": v(37.5, -81.75) * mm, "radius": 1.75 * mm});
            skCircle(sketch, "E225.0", {"center": v(-37.5, -81.75) * mm, "radius": 1.75 * mm});
            skSolve(sketch);
        }
        {
            var Q0;
            Q0 = qSketchRegion(id + "F29", true);
            extrude(context, id + "F30", {"entities" : qUnion([Q0]), "operationType" : NewBodyOperationType.REMOVE, "endBound" : BoundingType.THROUGH_ALL, "oppositeDirection" : true, "depth" : 25 * mm});
        }
        {
            var Q0;
            Q0=makeQuery(id+"F26.opExtrude","SWEPT_EDGE",EDGE,{"disambiguationData":[OSD([sQuery(id+"F25.wireOp",EDGE,"E216"),sQuery(id+"F25.wireOp",EDGE,"E217")])]});
            fillet(context, id + "F31", {"entities" : qUnion([Q0]), "radius" : 6 * mm, "tangentPropagation" : true, "allowEdgeOverflow" : false});
        }
        {
            var Q0;
            Q0=makeQuery(id+"F26.opExtrude","SWEPT_EDGE",EDGE,{"disambiguationData":[OSD([sQuery(id+"F25.wireOp",EDGE,"E215"),sQuery(id+"F25.wireOp",EDGE,"E217")])]});
            fillet(context, id + "F32", {"entities" : qUnion([Q0]), "radius" : 6 * mm, "tangentPropagation" : true, "allowEdgeOverflow" : false});
        }
        {
            var Q0;
            Q0=makeQuery(id+"F18.opExtrude","CAP_FACE",FACE,{"disambiguationData":[OSD([sQuery(id+"F1.wireOp",EDGE,"E138.0"),sQuery(id+"F8.wireOp",EDGE,"E172.bottom"),sQuery(id+"F8.wireOp",EDGE,"E172.top"),sQuery(id+"F8.wireOp",EDGE,"E172.left"),sQuery(id+"F8.wireOp",EDGE,"E172.right"),sQuery(id+"F8.wireOp",EDGE,"E173.0"),sQuery(id+"F8.wireOp",EDGE,"E174.trimOffspring")])],"isStart":false});
            var sketch = newSketch(context, id + "F33", { "sketchPlane" : qUnion([Q0])});
            skCircle(sketch, "E226.0", {"center": v(37.5, 81.75) * mm, "radius": 1.75 * mm, "construction": true});
            skCircle(sketch, "E227.0", {"center": v(0, 81.75) * mm, "radius": 1.75 * mm, "construction": true});
            skCircle(sketch, "E228.0", {"center": v(-37.5, 81.75) * mm, "radius": 1.75 * mm, "construction": true});
            skCircle(sketch, "E229", {"center": v(37.5, 81.75) * mm, "radius": 3 * mm});
            skCircle(sketch, "E230", {"center": v(0, 81.75) * mm, "radius": 3 * mm});
            skCircle(sketch, "E231", {"center": v(-37.5, 81.75) * mm, "radius": 3 * mm});
            skSolve(sketch);
        }
        {
            var Q0;
            Q0 = qSketchRegion(id + "F33", true);
            extrude(context, id + "F34", {"entities" : qUnion([Q0]), "operationType" : NewBodyOperationType.REMOVE, "depth" : 20 * mm, "hasSecondDirection" : true, "secondDirectionOppositeDirection" : false, "secondDirectionDepth" : 11.5 * mm});
        }
        {
            var Q0;
            Q0=makeQuery(id+"F28.boolean.opBoolean","MERGE",FACE,{"derivedFrom":[makeQuery(id+"F26.opExtrude","CAP_FACE",FACE,{"disambiguationData":[OSD([sQuery(id+"F25.wireOp",EDGE,"E211"),sQuery(id+"F25.wireOp",EDGE,"E213"),sQuery(id+"F25.wireOp",EDGE,"E214"),sQuery(id+"F25.wireOp",EDGE,"E215"),sQuery(id+"F25.wireOp",EDGE,"E216"),sQuery(id+"F25.wireOp",EDGE,"E217")])],"isStart":false}),makeQuery(id+"F28.opExtrude","CAP_FACE",FACE,{"disambiguationData":[OSD([sQuery(id+"F27.wireOp",EDGE,"E218.0"),sQuery(id+"F27.wireOp",EDGE,"E219.0"),sQuery(id+"F27.wireOp",EDGE,"E220"),sQuery(id+"F27.wireOp",EDGE,"E221"),sQuery(id+"F27.wireOp",EDGE,"E222")])],"isStart":true})]});
            var sketch = newSketch(context, id + "F35", { "sketchPlane" : qUnion([Q0])});
            skLineSegment(sketch, "E232.0", {"start": v(-93.75, 5) * mm, "end": v(-97.73, 4.3) * mm});
            skLineSegment(sketch, "E233", {"start": v(-93.55, -19.4) * mm, "end": v(-89.57, -18.7) * mm});
            skLineSegment(sketch, "E234", {"start": v(-89.57, -18.7) * mm, "end": v(-87.83, -28.56) * mm});
            skLineSegment(sketch, "E235", {"start": v(-93.55, -19.4) * mm, "end": v(-91.81, -29.26) * mm});
            skLineSegment(sketch, "E236", {"start": v(-91.81, -29.26) * mm, "end": v(-87.83, -28.56) * mm});
            skLineSegment(sketch, "E237", {"start": v(-93.75, 5) * mm, "end": v(-95.49, 14.85) * mm});
            skLineSegment(sketch, "E238", {"start": v(-95.49, 14.85) * mm, "end": v(-99.47, 14.15) * mm});
            skLineSegment(sketch, "E239", {"start": v(-99.47, 14.15) * mm, "end": v(-97.73, 4.3) * mm});
            skSolve(sketch);
        }
        {
            var Q0;
            Q0 = qSketchRegion(id + "F35", true);
            var Q1;
            Q1=makeQuery(id+"F28.boolean.opBoolean","MERGE",FACE,{"derivedFrom":[makeQuery(id+"F26.opExtrude","CAP_FACE",FACE,{"disambiguationData":[OSD([sQuery(id+"F25.wireOp",EDGE,"E211"),sQuery(id+"F25.wireOp",EDGE,"E213"),sQuery(id+"F25.wireOp",EDGE,"E214"),sQuery(id+"F25.wireOp",EDGE,"E215"),sQuery(id+"F25.wireOp",EDGE,"E216"),sQuery(id+"F25.wireOp",EDGE,"E217")])],"isStart":true}),makeQuery(id+"F28.opExtrude","CAP_FACE",FACE,{"disambiguationData":[OSD([sQuery(id+"F27.wireOp",EDGE,"E218.0"),sQuery(id+"F27.wireOp",EDGE,"E219.0"),sQuery(id+"F27.wireOp",EDGE,"E220"),sQuery(id+"F27.wireOp",EDGE,"E221"),sQuery(id+"F27.wireOp",EDGE,"E222")])],"isStart":false})]});
            extrude(context, id + "F36", {"entities" : qUnion([Q0]), "operationType" : NewBodyOperationType.ADD, "endBound" : BoundingType.UP_TO_SURFACE, "oppositeDirection" : true, "endBoundEntityFace" : qUnion([Q1]), "depth" : 25 * mm});
        }
        {
            var Q0;
            Q0=makeQuery(id+"F36.opExtrude","SWEPT_FACE",FACE,{"disambiguationData":[OSD([sQuery(id+"F35.wireOp",EDGE,"E237")])]});
            var sketch = newSketch(context, id + "F37", { "sketchPlane" : qUnion([Q0])});
            skLineSegment(sketch, "E240", {"start": v(50, 31.2) * mm, "end": v(50, 61.2) * mm});
            skLineSegment(sketch, "E241", {"start": v(50, 61.2) * mm, "end": v(35, 61.2) * mm});
            skLineSegment(sketch, "E242", {"start": v(35, 61.2) * mm, "end": v(35, 31.2) * mm});
            skLineSegment(sketch, "E243", {"start": v(50, 31.2) * mm, "end": v(35, 31.2) * mm});
            skLineSegment(sketch, "E244.0", {"start": v(50, -12.87) * mm, "end": v(-50, -12.87) * mm, "construction": true});
            skLineSegment(sketch, "E245.0", {"start": v(50, 31.2) * mm, "end": v(-50, 31.2) * mm, "construction": true});
            skLineSegment(sketch, "E246", {"start": v(50, -12.87) * mm, "end": v(50, -42.87) * mm});
            skLineSegment(sketch, "E247", {"start": v(50, -42.87) * mm, "end": v(35, -42.87) * mm});
            skLineSegment(sketch, "E248", {"start": v(35, -42.87) * mm, "end": v(35, -12.87) * mm});
            skLineSegment(sketch, "E249", {"start": v(35, -12.87) * mm, "end": v(50, -12.87) * mm});
            skLineSegment(sketch, "E250", {"start": v(7.5, 31.2) * mm, "end": v(-7.5, 31.2) * mm});
            skLineSegment(sketch, "E251", {"start": v(-7.5, 31.2) * mm, "end": v(-7.5, 61.2) * mm});
            skLineSegment(sketch, "E252", {"start": v(-7.5, 61.2) * mm, "end": v(7.5, 61.2) * mm});
            skLineSegment(sketch, "E253", {"start": v(7.5, 61.2) * mm, "end": v(7.5, 31.2) * mm});
            skLineSegment(sketch, "E254", {"start": v(78.3, 9.17) * mm, "end": v(-87.4, 9.17) * mm, "construction": true});
            skLineSegment(sketch, "E255.MirrorCS", {"start": v(-7.5, -12.87) * mm, "end": v(-7.5, -42.87) * mm});
            skLineSegment(sketch, "E256.MirrorCS", {"start": v(7.5, -12.87) * mm, "end": v(-7.5, -12.87) * mm});
            skLineSegment(sketch, "E257.MirrorCS", {"start": v(7.5, -42.87) * mm, "end": v(7.5, -12.87) * mm});
            skLineSegment(sketch, "E258.MirrorCS", {"start": v(-7.5, -42.87) * mm, "end": v(7.5, -42.87) * mm});
            skLineSegment(sketch, "E259.MirrorCS", {"start": v(-35, -12.87) * mm, "end": v(-50, -12.87) * mm});
            skLineSegment(sketch, "E260.MirrorCS", {"start": v(-50, 31.2) * mm, "end": v(-35, 31.2) * mm});
            skLineSegment(sketch, "E261.MirrorCS", {"start": v(-50, 31.2) * mm, "end": v(-50, 61.2) * mm});
            skLineSegment(sketch, "E262.MirrorCS", {"start": v(-50, 61.2) * mm, "end": v(-35, 61.2) * mm});
            skLineSegment(sketch, "E263.MirrorCS", {"start": v(-50, -12.87) * mm, "end": v(-50, -42.87) * mm});
            skLineSegment(sketch, "E264.MirrorCS", {"start": v(-35, -42.87) * mm, "end": v(-35, -12.87) * mm});
            skLineSegment(sketch, "E265.MirrorCS", {"start": v(-35, 61.2) * mm, "end": v(-35, 31.2) * mm});
            skLineSegment(sketch, "E266.MirrorCS", {"start": v(-50, -42.87) * mm, "end": v(-35, -42.87) * mm});
            skSolve(sketch);
        }
        {
            var Q0;
            Q0 = qSketchRegion(id + "F37", true);
            var Q1;
            Q1=makeQuery(id+"F36.boolean.opBoolean","MERGE",FACE,{"derivedFrom":[makeQuery(id+"F28.opExtrude","SWEPT_FACE",FACE,{"disambiguationData":[OSD([sQuery(id+"F27.wireOp",EDGE,"E221")])]}),makeQuery(id+"F36.opExtrude","SWEPT_FACE",FACE,{"disambiguationData":[OSD([sQuery(id+"F35.wireOp",EDGE,"E235")])]}),makeQuery(id+"F36.opExtrude","SWEPT_FACE",FACE,{"disambiguationData":[OSD([sQuery(id+"F35.wireOp",EDGE,"E239")])]})]});
            extrude(context, id + "F38", {"entities" : qUnion([Q0]), "operationType" : NewBodyOperationType.ADD, "endBound" : BoundingType.UP_TO_SURFACE, "oppositeDirection" : true, "endBoundEntityFace" : qUnion([Q1]), "depth" : 25 * mm});
        }
        {
            var Q0;
            Q0=makeQuery(id+"F38.opExtrude","SWEPT_EDGE",EDGE,{"disambiguationData":[OSD([sQuery(id+"F37.wireOp",EDGE,"E241"),sQuery(id+"F37.wireOp",EDGE,"E242")])]});
            var Q1;
            Q1=makeQuery(id+"F38.opExtrude","SWEPT_EDGE",EDGE,{"disambiguationData":[OSD([sQuery(id+"F37.wireOp",EDGE,"E240"),sQuery(id+"F37.wireOp",EDGE,"E241")])]});
            var Q2;
            Q2=makeQuery(id+"F38.opExtrude","SWEPT_EDGE",EDGE,{"disambiguationData":[OSD([sQuery(id+"F37.wireOp",EDGE,"E252"),sQuery(id+"F37.wireOp",EDGE,"E253")])]});
            var Q3;
            Q3=makeQuery(id+"F38.opExtrude","SWEPT_EDGE",EDGE,{"disambiguationData":[OSD([sQuery(id+"F37.wireOp",EDGE,"E251"),sQuery(id+"F37.wireOp",EDGE,"E252")])]});
            var Q4;
            Q4=makeQuery(id+"F38.opExtrude","SWEPT_EDGE",EDGE,{"disambiguationData":[OSD([sQuery(id+"F37.wireOp",EDGE,"E261.MirrorCS"),sQuery(id+"F37.wireOp",EDGE,"E262.MirrorCS")])]});
            var Q5;
            Q5=makeQuery(id+"F38.opExtrude","SWEPT_EDGE",EDGE,{"disambiguationData":[OSD([sQuery(id+"F37.wireOp",EDGE,"E262.MirrorCS"),sQuery(id+"F37.wireOp",EDGE,"E265.MirrorCS")])]});
            var Q6;
            Q6=makeQuery(id+"F38.opExtrude","SWEPT_EDGE",EDGE,{"disambiguationData":[OSD([sQuery(id+"F37.wireOp",EDGE,"E263.MirrorCS"),sQuery(id+"F37.wireOp",EDGE,"E266.MirrorCS")])]});
            var Q7;
            Q7=makeQuery(id+"F38.opExtrude","SWEPT_EDGE",EDGE,{"disambiguationData":[OSD([sQuery(id+"F37.wireOp",EDGE,"E264.MirrorCS"),sQuery(id+"F37.wireOp",EDGE,"E266.MirrorCS")])]});
            var Q8;
            Q8=makeQuery(id+"F38.opExtrude","SWEPT_EDGE",EDGE,{"disambiguationData":[OSD([sQuery(id+"F37.wireOp",EDGE,"E255.MirrorCS"),sQuery(id+"F37.wireOp",EDGE,"E258.MirrorCS")])]});
            var Q9;
            Q9=makeQuery(id+"F38.opExtrude","SWEPT_EDGE",EDGE,{"disambiguationData":[OSD([sQuery(id+"F37.wireOp",EDGE,"E257.MirrorCS"),sQuery(id+"F37.wireOp",EDGE,"E258.MirrorCS")])]});
            var Q10;
            Q10=makeQuery(id+"F38.opExtrude","SWEPT_EDGE",EDGE,{"disambiguationData":[OSD([sQuery(id+"F37.wireOp",EDGE,"E247"),sQuery(id+"F37.wireOp",EDGE,"E248")])]});
            var Q11;
            Q11=makeQuery(id+"F38.opExtrude","SWEPT_EDGE",EDGE,{"disambiguationData":[OSD([sQuery(id+"F37.wireOp",EDGE,"E246"),sQuery(id+"F37.wireOp",EDGE,"E247")])]});
            var Q12;
            Q12=makeQuery(id+"F38.opExtrude","SWEPT_EDGE",EDGE,{"disambiguationData":[OSD([sQuery(id+"F35.wireOp",EDGE,"E237"),sQuery(id+"F35.wireOp",EDGE,"E238"),sQuery(id+"F37.wireOp",EDGE,"E242"),sQuery(id+"F37.wireOp",EDGE,"E243")])]});
            var Q13;
            Q13=makeQuery(id+"F38.opExtrude","SWEPT_EDGE",EDGE,{"disambiguationData":[OSD([sQuery(id+"F35.wireOp",EDGE,"E237"),sQuery(id+"F35.wireOp",EDGE,"E238"),sQuery(id+"F37.wireOp",EDGE,"E250"),sQuery(id+"F37.wireOp",EDGE,"E253")])]});
            var Q14;
            Q14=makeQuery(id+"F38.opExtrude","SWEPT_EDGE",EDGE,{"disambiguationData":[OSD([sQuery(id+"F35.wireOp",EDGE,"E237"),sQuery(id+"F35.wireOp",EDGE,"E238"),sQuery(id+"F37.wireOp",EDGE,"E260.MirrorCS"),sQuery(id+"F37.wireOp",EDGE,"E265.MirrorCS")])]});
            var Q15;
            Q15=makeQuery(id+"F38.opExtrude","SWEPT_EDGE",EDGE,{"disambiguationData":[OSD([sQuery(id+"F35.wireOp",EDGE,"E237"),sQuery(id+"F35.wireOp",EDGE,"E238"),sQuery(id+"F37.wireOp",EDGE,"E250"),sQuery(id+"F37.wireOp",EDGE,"E251")])]});
            var Q16;
            Q16=makeQuery(id+"F38.opExtrude","SWEPT_EDGE",EDGE,{"disambiguationData":[OSD([sQuery(id+"F37.wireOp",EDGE,"E248"),sQuery(id+"F37.wireOp",EDGE,"E249")])]});
            var Q17;
            Q17=makeQuery(id+"F38.opExtrude","SWEPT_EDGE",EDGE,{"disambiguationData":[OSD([sQuery(id+"F37.wireOp",EDGE,"E256.MirrorCS"),sQuery(id+"F37.wireOp",EDGE,"E257.MirrorCS")])]});
            var Q18;
            Q18=makeQuery(id+"F38.opExtrude","SWEPT_EDGE",EDGE,{"disambiguationData":[OSD([sQuery(id+"F37.wireOp",EDGE,"E255.MirrorCS"),sQuery(id+"F37.wireOp",EDGE,"E256.MirrorCS")])]});
            var Q19;
            Q19=makeQuery(id+"F38.opExtrude","SWEPT_EDGE",EDGE,{"disambiguationData":[OSD([sQuery(id+"F37.wireOp",EDGE,"E259.MirrorCS"),sQuery(id+"F37.wireOp",EDGE,"E264.MirrorCS")])]});
            fillet(context, id + "F39", {"entities" : qUnion([Q0, Q1, Q2, Q3, Q4, Q5, Q6, Q7, Q8, Q9, Q10, Q11, Q12, Q13, Q14, Q15, Q16, Q17, Q18, Q19]), "radius" : 5 * mm, "tangentPropagation" : true, "allowEdgeOverflow" : false});
        }
        {
            var Q0;
            Q0=makeQuery(id+"F18.opExtrude","CAP_FACE",FACE,{"disambiguationData":[OSD([sQuery(id+"F1.wireOp",EDGE,"E138.0"),sQuery(id+"F8.wireOp",EDGE,"E172.bottom"),sQuery(id+"F8.wireOp",EDGE,"E172.top"),sQuery(id+"F8.wireOp",EDGE,"E172.left"),sQuery(id+"F8.wireOp",EDGE,"E172.right"),sQuery(id+"F8.wireOp",EDGE,"E173.0"),sQuery(id+"F8.wireOp",EDGE,"E174.trimOffspring")])],"isStart":false});
            chamfer(context, id + "F40", {"entities" : qUnion([Q0]), "width" : 0.5 * mm, "tangentPropagation" : true});
        }
        {
            var Q0;
            {var subQ0=sQuery(id+"F35.wireOp",EDGE,"E239");var subQ1=sQuery(id+"F35.wireOp",EDGE,"E235");var subQ2=sQuery(id+"F27.wireOp",EDGE,"E221");Q0=makeQuery(id+"F38.boolean.opBoolean","MERGE",FACE,{"derivedFrom":[makeQuery(id+"F36.boolean.opBoolean","MERGE",FACE,{"derivedFrom":[makeQuery(id+"F28.opExtrude","SWEPT_FACE",FACE,{"disambiguationData":[OSD([subQ2])]}),makeQuery(id+"F36.opExtrude","SWEPT_FACE",FACE,{"disambiguationData":[OSD([subQ1])]}),makeQuery(id+"F36.opExtrude","SWEPT_FACE",FACE,{"disambiguationData":[OSD([subQ0])]})]}),makeQuery(id+"F38.opExtrude","CAP_FACE",FACE,{"disambiguationData":[OSD([subQ2,subQ1,subQ0]),ownerDisambiguation([makeQuery(id+"F37.imprint","IMPRINT",EDGE,{"derivedFrom":sQuery(id+"F37.wireOp",EDGE,"E240")})])],"isStart":false}),makeQuery(id+"F38.opExtrude","CAP_FACE",FACE,{"disambiguationData":[OSD([subQ2,subQ1,subQ0]),ownerDisambiguation([makeQuery(id+"F37.imprint","IMPRINT",EDGE,{"derivedFrom":sQuery(id+"F37.wireOp",EDGE,"E246")})])],"isStart":false}),makeQuery(id+"F38.opExtrude","CAP_FACE",FACE,{"disambiguationData":[OSD([subQ2,subQ1,subQ0]),ownerDisambiguation([makeQuery(id+"F37.imprint","IMPRINT",EDGE,{"derivedFrom":sQuery(id+"F37.wireOp",EDGE,"E250")})])],"isStart":false}),makeQuery(id+"F38.opExtrude","CAP_FACE",FACE,{"disambiguationData":[OSD([subQ2,subQ1,subQ0]),ownerDisambiguation([makeQuery(id+"F37.imprint","IMPRINT",EDGE,{"derivedFrom":sQuery(id+"F37.wireOp",EDGE,"E255.MirrorCS")})])],"isStart":false}),makeQuery(id+"F38.opExtrude","CAP_FACE",FACE,{"disambiguationData":[OSD([subQ2,subQ1,subQ0]),ownerDisambiguation([makeQuery(id+"F37.imprint","IMPRINT",EDGE,{"derivedFrom":sQuery(id+"F37.wireOp",EDGE,"E259.MirrorCS")})])],"isStart":false}),makeQuery(id+"F38.opExtrude","CAP_FACE",FACE,{"disambiguationData":[OSD([subQ2,subQ1,subQ0]),ownerDisambiguation([makeQuery(id+"F37.imprint","IMPRINT",EDGE,{"derivedFrom":sQuery(id+"F37.wireOp",EDGE,"E260.MirrorCS")})])],"isStart":false})]});}
            chamfer(context, id + "F41", {"entities" : qUnion([Q0]), "width" : 0.5 * mm, "tangentPropagation" : true});
        }
    });
